FCSTD DOCUMENT  (FreeCAD 1.0R39109 (Git))
Label: seat_mover
License: All rights reserved
LicenseURL: https://en.wikipedia.org/wiki/All_rights_reserved
objects: App::Link×73, App::FeaturePython×3, Assembly::AssemblyLink×3, Assembly::JointGroup×1, Assembly::AssemblyObject×1
EXTERNAL_REF file=surge_platform.FCStd obj=Assembly
EXTERNAL_REF file=surge_platform.FCStd obj=linear_shaft_25x500
EXTERNAL_REF file=surge_platform.FCStd obj=linear_shaft_25x501
EXTERNAL_REF file=surge_platform.FCStd obj=SHF25
EXTERNAL_REF file=surge_platform.FCStd obj=SHF026
EXTERNAL_REF file=surge_platform.FCStd obj=SHF027
EXTERNAL_REF file=surge_platform.FCStd obj=SHF028
EXTERNAL_REF file=surge_platform.FCStd obj=_0ST_M02438
EXTERNAL_REF file=surge_platform.FCStd obj=SFU1605_ball_screw_250mm
EXTERNAL_REF file=surge_platform.FCStd obj=BK12
EXTERNAL_REF file=surge_platform.FCStd obj=coupler_10x19
EXTERNAL_REF file=surge_platform.FCStd obj=profile_40x40x500
EXTERNAL_REF file=surge_platform.FCStd obj=profile_40x40x501
EXTERNAL_REF file=surge_platform.FCStd obj=corner_bracket_40x40
EXTERNAL_REF file=surge_platform.FCStd obj=corner_bracket_40x041
EXTERNAL_REF file=surge_platform.FCStd obj=corner_bracket_40x042
EXTERNAL_REF file=surge_platform.FCStd obj=corner_bracket_40x043
EXTERNAL_REF file=sway_platform.FCStd obj=Assembly
EXTERNAL_REF file=sway_platform.FCStd obj=SC25UU_to_SH25
EXTERNAL_REF file=sway_platform.FCStd obj=SC25UU_to_SH026
EXTERNAL_REF file=sway_platform.FCStd obj=SC25UU
EXTERNAL_REF file=sway_platform.FCStd obj=SC25UU001
EXTERNAL_REF file=sway_platform.FCStd obj=SC25UU002
EXTERNAL_REF file=sway_platform.FCStd obj=SC25UU003
EXTERNAL_REF file=sway_platform.FCStd obj=SH25
EXTERNAL_REF file=sway_platform.FCStd obj=SH026
EXTERNAL_REF file=sway_platform.FCStd obj=SH027
EXTERNAL_REF file=sway_platform.FCStd obj=SH028
EXTERNAL_REF file=sway_platform.FCStd obj=linear_shaft_25x428
EXTERNAL_REF file=sway_platform.FCStd obj=linear_shaft_25x429
EXTERNAL_REF file=sway_platform.FCStd obj=SH029
EXTERNAL_REF file=sway_platform.FCStd obj=DSG16H_to_SH25
EXTERNAL_REF file=sway_platform.FCStd obj=DSG16H
EXTERNAL_REF file=sway_platform.FCStd obj=SFU1605_ball_screw_nut
EXTERNAL_REF file=sway_platform.FCStd obj=_0ST_M02438
EXTERNAL_REF file=sway_platform.FCStd obj=coupler_10x19
EXTERNAL_REF file=sway_platform.FCStd obj=SFU1605_ball_screw_250mm
EXTERNAL_REF file=sway_platform.FCStd obj=BK12
EXTERNAL_REF file=seat_platform.FCStd obj=Assembly
EXTERNAL_REF file=seat_platform.FCStd obj=SC25UU
EXTERNAL_REF file=seat_platform.FCStd obj=SC25UU001
EXTERNAL_REF file=seat_platform.FCStd obj=SC25UU002
EXTERNAL_REF file=seat_platform.FCStd obj=SC25UU003
EXTERNAL_REF file=seat_platform.FCStd obj=profile_40x40x310
EXTERNAL_REF file=seat_platform.FCStd obj=profile_40x40x311
EXTERNAL_REF file=seat_platform.FCStd obj=corner_bracket_40x40
EXTERNAL_REF file=seat_platform.FCStd obj=corner_bracket_40x041
EXTERNAL_REF file=seat_platform.FCStd obj=corner_bracket_40x042
EXTERNAL_REF file=seat_platform.FCStd obj=corner_bracket_40x043
EXTERNAL_REF file=seat_platform.FCStd obj=corner_bracket_40x044
EXTERNAL_REF file=seat_platform.FCStd obj=corner_bracket_40x045
EXTERNAL_REF file=seat_platform.FCStd obj=corner_bracket_40x046
EXTERNAL_REF file=seat_platform.FCStd obj=corner_bracket_40x047
EXTERNAL_REF file=seat_platform.FCStd obj=DSG16H_to_profile_40x40
EXTERNAL_REF file=seat_platform.FCStd obj=DSG16H
EXTERNAL_REF file=seat_platform.FCStd obj=SFU1605_ball_screw_nut
EXTERNAL_REF file=seat_platform.FCStd obj=profile_40x40x270
EXTERNAL_REF file=seat_platform.FCStd obj=profile_40x40x312
EXTERNAL_REF file=seat_platform.FCStd obj=corner_bracket_40x048
EXTERNAL_REF file=seat_platform.FCStd obj=corner_bracket_40x049
EXTERNAL_REF file=seat_platform.FCStd obj=corner_bracket_40x050
EXTERNAL_REF file=seat_platform.FCStd obj=corner_bracket_40x051
EXTERNAL_REF file=seat_platform.FCStd obj=seat
EXTERNAL_REF file=surge_platform.FCStd obj=surge_motor_mount_side
EXTERNAL_REF file=surge_platform.FCStd obj=surge_motor_mount_bottom
EXTERNAL_REF file=surge_platform.FCStd obj=surge_motor_mount_top
EXTERNAL_REF file=sway_platform.FCStd obj=sway_SC25UU_to_SH25_with_plate
EXTERNAL_REF file=sway_platform.FCStd obj=sway_motor_mount_rear_plate
EXTERNAL_REF file=sway_platform.FCStd obj=sway_SC25UU_to_SH25_with_plate001
EXTERNAL_REF file=sway_platform.FCStd obj=sway_motor_mount_front_plate
EXTERNAL_REF file=sway_platform.FCStd obj=sway_motor_mount_front_plate_shaft_support
EXTERNAL_REF file=sway_platform.FCStd obj=sway_motor_mount_side
EXTERNAL_REF file=sway_platform.FCStd obj=sway_motor_mount_top
EXTERNAL_REF file=sway_platform.FCStd obj=sway_motor_mount_bottom
EXTERNAL_REF file=surge_platform.FCStd obj=surge_BK12_mount_bottom
EXTERNAL_REF file=surge_platform.FCStd obj=surge_BK12_mount_top

FEATURE [App::Link] linear_shaft_25x500  label="linear_shaft_25x500_right"
  LinkPlacement = pos=(404,2.64e-14,1.8225e-12) rot=(0,0,1;0rad)
  LinkedObject = -> <external surge_platform.FCStd>#linear_shaft_25x500
  Placement = pos=(404,2.64e-14,1.8225e-12) rot=(0,0,1;0rad)
FEATURE [App::Link] linear_shaft_25x501  label="linear_shaft_25x50_left"
  LinkPlacement = pos=(0,0,1.819e-12) rot=(0,0,1;0rad)
  LinkedObject = -> <external surge_platform.FCStd>#linear_shaft_25x501
  Placement = pos=(0,0,1.819e-12) rot=(0,0,1;0rad)
FEATURE [App::Link] SHF25  label="SHF25_000"
  LinkPlacement = pos=(10,-527.778,-1.55556) rot=(0,0.707107,0.707107;3.14159rad)
  LinkedObject = -> <external surge_platform.FCStd>#SHF25
  Placement = pos=(10,-527.778,-1.55556) rot=(0,0.707107,0.707107;3.14159rad)
FEATURE [App::Link] SHF026  label="SHF25_001"
  LinkPlacement = pos=(-10,27.7778,-1.55556) rot=(1,0,0;1.5708rad)
  LinkedObject = -> <external surge_platform.FCStd>#SHF026
  Placement = pos=(-10,27.7778,-1.55556) rot=(1,0,0;1.5708rad)
FEATURE [App::Link] SHF027  label="SHF25_002"
  LinkPlacement = pos=(414,-527.778,-1.55556) rot=(0,0.707107,0.707107;3.14159rad)
  LinkedObject = -> <external surge_platform.FCStd>#SHF027
  Placement = pos=(414,-527.778,-1.55556) rot=(0,0.707107,0.707107;3.14159rad)
FEATURE [App::Link] SHF028  label="SHF25_003"
  LinkPlacement = pos=(394,27.7778,-1.55556) rot=(1,0,0;1.5708rad)
  LinkedObject = -> <external surge_platform.FCStd>#SHF028
  Placement = pos=(394,27.7778,-1.55556) rot=(1,0,0;1.5708rad)
FEATURE [App::Link] _0ST_M02438  label="80ST-M02438"
  LinkPlacement = pos=(202,-341.4,4.5) rot=(-1,0,0;1.5708rad)
  LinkedObject = -> <external surge_platform.FCStd>#_0ST_M02438
  Placement = pos=(202,-341.4,4.5) rot=(-1,0,0;1.5708rad)
FEATURE [App::Link] SFU1605_ball_screw_250mm
  LinkPlacement = pos=(202,-492.9,4.5) rot=(1,0,0;1.5708rad)
  LinkedObject = -> <external surge_platform.FCStd>#SFU1605_ball_screw_250mm
  Placement = pos=(202,-492.9,4.5) rot=(1,0,0;1.5708rad)
FEATURE [App::Link] BK12
  LinkPlacement = pos=(202,-235.65,-20.5) rot=(0,0,1;0rad)
  LinkedObject = -> <external surge_platform.FCStd>#BK12
  Placement = pos=(202,-235.65,-20.5) rot=(0,0,1;0rad)
FEATURE [App::Link] coupler_10x19
  LinkPlacement = pos=(202,-261.9,4.5) rot=(0,0,1;0rad)
  LinkedObject = -> <external surge_platform.FCStd>#coupler_10x19
  Placement = pos=(202,-261.9,4.5) rot=(0,0,1;0rad)
FEATURE [App::Link] profile_40x40x500  label="profile_40x40x500_right"
  LinkPlacement = pos=(262,-150,1.783e-12) rot=(0,0.707107,-0.707107;3.14159rad)
  LinkedObject = -> <external surge_platform.FCStd>#profile_40x40x500
  Placement = pos=(262,-150,1.783e-12) rot=(0,0.707107,-0.707107;3.14159rad)
FEATURE [App::Link] profile_40x40x501  label="profile_40x40x500_left"
  LinkPlacement = pos=(142,-150,1.783e-12) rot=(0,0.707107,-0.707107;3.14159rad)
  LinkedObject = -> <external surge_platform.FCStd>#profile_40x40x501
  Placement = pos=(142,-150,1.783e-12) rot=(0,0.707107,-0.707107;3.14159rad)
FEATURE [App::Link] corner_bracket_40x40  label="corner_bracket_40x40_000"
  LinkPlacement = pos=(142,-587.433,56) rot=(0,1,0;1.5708rad)
  LinkedObject = -> <external surge_platform.FCStd>#corner_bracket_40x40
  Placement = pos=(142,-587.433,56) rot=(0,1,0;1.5708rad)
FEATURE [App::Link] corner_bracket_40x041  label="corner_bracket_40x40_001"
  LinkPlacement = pos=(142,-36,-67.4326) rot=(0.57735,0.57735,0.57735;2.0944rad)
  LinkedObject = -> <external surge_platform.FCStd>#corner_bracket_40x041
  Placement = pos=(142,-36,-67.4326) rot=(0.57735,0.57735,0.57735;2.0944rad)
FEATURE [App::Link] corner_bracket_40x042  label="corner_bracket_40x40_002"
  LinkPlacement = pos=(262,-587.433,56) rot=(0,1,0;1.5708rad)
  LinkedObject = -> <external surge_platform.FCStd>#corner_bracket_40x042
  Placement = pos=(262,-587.433,56) rot=(0,1,0;1.5708rad)
FEATURE [App::Link] corner_bracket_40x043  label="corner_bracket_40x40_003"
  LinkPlacement = pos=(262,-36,67.4326) rot=(0.57735,0.57735,-0.57735;4.18879rad)
  LinkedObject = -> <external surge_platform.FCStd>#corner_bracket_40x043
  Placement = pos=(262,-36,67.4326) rot=(0.57735,0.57735,-0.57735;4.18879rad)
FEATURE [App::Link] SC25UU_to_SH25  label="SC25UU_to_SH25_000"
  LinkedObject = -> <external sway_platform.FCStd>#SC25UU_to_SH25
FEATURE [App::Link] SC25UU_to_SH026  label="SC25UU_to_SH25_001"
  LinkPlacement = pos=(1e-15,204,-1e-16) rot=(0,0,1;0rad)
  LinkedObject = -> <external sway_platform.FCStd>#SC25UU_to_SH026
  Placement = pos=(1e-15,204,-1e-16) rot=(0,0,1;0rad)
FEATURE [App::Link] SC25UU  label="SC25UU_000"
  LinkPlacement = pos=(38,67,-415.5) rot=(1,0,0;1.5708rad)
  LinkedObject = -> <external sway_platform.FCStd>#SC25UU
  Placement = pos=(38,67,-415.5) rot=(1,0,0;1.5708rad)
FEATURE [App::Link] SC25UU001  label="SC25UU_001"
  LinkPlacement = pos=(38,271,-415.5) rot=(1,0,0;1.5708rad)
  LinkedObject = -> <external sway_platform.FCStd>#SC25UU001
  Placement = pos=(38,271,-415.5) rot=(1,0,0;1.5708rad)
FEATURE [App::Link] SC25UU002  label="SC25UU_002"
  LinkPlacement = pos=(442,67,-415.5) rot=(1,0,0;1.5708rad)
  LinkedObject = -> <external sway_platform.FCStd>#SC25UU002
  Placement = pos=(442,67,-415.5) rot=(1,0,0;1.5708rad)
FEATURE [App::Link] SC25UU003  label="SC25UU_003"
  LinkPlacement = pos=(442,271,-415.5) rot=(1,0,0;1.5708rad)
  LinkedObject = -> <external sway_platform.FCStd>#SC25UU003
  Placement = pos=(442,271,-415.5) rot=(1,0,0;1.5708rad)
FEATURE [App::Link] SH25  label="SH25_000"
  LinkPlacement = pos=(-901.062,343.027,-226.938) rot=(0,0,1;0rad)
  LinkedObject = -> <external sway_platform.FCStd>#SH25
  Placement = pos=(-901.062,343.027,-226.938) rot=(0,0,1;0rad)
FEATURE [App::Link] SH026  label="SH25_001"
  LinkPlacement = pos=(977.062,-72.0272,-226.938) rot=(0,0,1;3.14159rad)
  LinkedObject = -> <external sway_platform.FCStd>#SH026
  Placement = pos=(977.062,-72.0272,-226.938) rot=(0,0,1;3.14159rad)
FEATURE [App::Link] SH027  label="SH25_002"
  LinkPlacement = pos=(-497.062,343.027,-226.938) rot=(0,0,1;0rad)
  LinkedObject = -> <external sway_platform.FCStd>#SH027
  Placement = pos=(-497.062,343.027,-226.938) rot=(0,0,1;0rad)
FEATURE [App::Link] SH028  label="SH25_003"
  LinkPlacement = pos=(1381.06,-72.0272,-226.938) rot=(0,0,1;3.14159rad)
  LinkedObject = -> <external sway_platform.FCStd>#SH028
  Placement = pos=(1381.06,-72.0272,-226.938) rot=(0,0,1;3.14159rad)
FEATURE [App::Link] linear_shaft_25x428  label="linear_shaft_25x428_front"
  LinkPlacement = pos=(454,33.5,45) rot=(0,0,-1;1.5708rad)
  LinkedObject = -> <external sway_platform.FCStd>#linear_shaft_25x428
  Placement = pos=(454,33.5,45) rot=(0,0,-1;1.5708rad)
FEATURE [App::Link] linear_shaft_25x429  label="linear_shaft_25x428_rear"
  LinkPlacement = pos=(454,237.5,45) rot=(0.707107,0.707107,0;3.14159rad)
  LinkedObject = -> <external sway_platform.FCStd>#linear_shaft_25x429
  Placement = pos=(454,237.5,45) rot=(0.707107,0.707107,0;3.14159rad)
FEATURE [App::Link] SH029  label="SH25_004"
  LinkPlacement = pos=(1179.06,-72.0272,-226.938) rot=(0,0,1;3.14159rad)
  LinkedObject = -> <external sway_platform.FCStd>#SH029
  Placement = pos=(1179.06,-72.0272,-226.938) rot=(0,0,1;3.14159rad)
FEATURE [App::Link] DSG16H_to_SH25
  LinkPlacement = pos=(215,218.5,-2) rot=(0,0,1;0rad)
  LinkedObject = -> <external sway_platform.FCStd>#DSG16H_to_SH25
  Placement = pos=(215,218.5,-2) rot=(0,0,1;0rad)
FEATURE [App::Link] DSG16H
  LinkPlacement = pos=(240,217.5,-22) rot=(0,0,1;0rad)
  LinkedObject = -> <external sway_platform.FCStd>#DSG16H
  Placement = pos=(240,217.5,-22) rot=(0,0,1;0rad)
FEATURE [App::Link] SFU1605_ball_screw_nut
  LinkPlacement = pos=(240,207.25,-22) rot=(0,-1,0;1.5708rad)
  LinkedObject = -> <external sway_platform.FCStd>#SFU1605_ball_screw_nut
  Placement = pos=(240,207.25,-22) rot=(0,-1,0;1.5708rad)
FEATURE [App::Link] _0ST_M02439  label="80ST-M02439"
  LinkPlacement = pos=(342.4,135.5,30) rot=(0.57735,-0.57735,-0.57735;2.0944rad)
  LinkedObject = -> <external sway_platform.FCStd>#_0ST_M02438
  Placement = pos=(342.4,135.5,30) rot=(0.57735,-0.57735,-0.57735;2.0944rad)
FEATURE [App::Link] coupler_10x020
  LinkPlacement = pos=(266.25,135.5,30) rot=(-0.57735,0.57735,0.57735;2.0944rad)
  LinkedObject = -> <external sway_platform.FCStd>#coupler_10x19
  Placement = pos=(266.25,135.5,30) rot=(-0.57735,0.57735,0.57735;2.0944rad)
FEATURE [App::Link] SFU1605_ball_screw_250mm001
  LinkPlacement = pos=(497.25,135.5,30) rot=(0.57735,0.57735,0.57735;2.0944rad)
  LinkedObject = -> <external sway_platform.FCStd>#SFU1605_ball_screw_250mm
  Placement = pos=(497.25,135.5,30) rot=(0.57735,0.57735,0.57735;2.0944rad)
FEATURE [App::Link] BK013
  LinkPlacement = pos=(240,135.5,55) rot=(0.707107,-0.707107,0;3.14159rad)
  LinkedObject = -> <external sway_platform.FCStd>#BK12
  Placement = pos=(240,135.5,55) rot=(0.707107,-0.707107,0;3.14159rad)
FEATURE [App::Link] SC25UU004  label="SC25UU_004"
  LinkPlacement = pos=(0,0,0) rot=(-0.57735,0.57735,0.57735;4.18879rad)
  LinkedObject = -> <external seat_platform.FCStd>#SC25UU
  Placement = pos=(0,0,0) rot=(-0.57735,0.57735,0.57735;4.18879rad)
FEATURE [App::Link] SC25UU005  label="SC25UU_005"
  LinkPlacement = pos=(-67,204,1.40432e-05) rot=(0.57735,0.57735,0.57735;2.0944rad)
  LinkedObject = -> <external seat_platform.FCStd>#SC25UU001
  Placement = pos=(-67,204,1.40432e-05) rot=(0.57735,0.57735,0.57735;2.0944rad)
FEATURE [App::Link] SC25UU006  label="SC25UU_006"
  LinkPlacement = pos=(136,-2.07725e-07,-2.78731e-05) rot=(0.57735,0.57735,0.57735;2.0944rad)
  LinkedObject = -> <external seat_platform.FCStd>#SC25UU002
  Placement = pos=(136,-2.07725e-07,-2.78731e-05) rot=(0.57735,0.57735,0.57735;2.0944rad)
FEATURE [App::Link] SC25UU007  label="SC25UU_007"
  LinkPlacement = pos=(203,204,-4.12931e-05) rot=(-0.57735,0.57735,0.57735;4.18879rad)
  LinkedObject = -> <external seat_platform.FCStd>#SC25UU003
  Placement = pos=(203,204,-4.12931e-05) rot=(-0.57735,0.57735,0.57735;4.18879rad)
FEATURE [App::Link] profile_40x40x310  label="profile_40x40x310_right"
  LinkPlacement = pos=(183,107,435.5) rot=(1,0,0;1.5708rad)
  LinkedObject = -> <external seat_platform.FCStd>#profile_40x40x310
  Placement = pos=(183,107,435.5) rot=(1,0,0;1.5708rad)
FEATURE [App::Link] profile_40x40x311  label="profile_40x40x310_left"
  LinkPlacement = pos=(-46.9999,107,435.5) rot=(1,0,0;1.5708rad)
  LinkedObject = -> <external seat_platform.FCStd>#profile_40x40x311
  Placement = pos=(-46.9999,107,435.5) rot=(1,0,0;1.5708rad)
FEATURE [App::Link] corner_bracket_40x044  label="corner_bracket_40x40_004"
  LinkPlacement = pos=(9.00006,-27,328.067) rot=(0,0.707107,0.707107;3.14159rad)
  LinkedObject = -> <external seat_platform.FCStd>#corner_bracket_40x40
  Placement = pos=(9.00006,-27,328.067) rot=(0,0.707107,0.707107;3.14159rad)
FEATURE [App::Link] corner_bracket_40x045  label="corner_bracket_40x40_005"
  LinkPlacement = pos=(9.00006,27,328.067) rot=(0,0.707107,0.707107;3.14159rad)
  LinkedObject = -> <external seat_platform.FCStd>#corner_bracket_40x041
  Placement = pos=(9.00006,27,328.067) rot=(0,0.707107,0.707107;3.14159rad)
FEATURE [App::Link] corner_bracket_40x046  label="corner_bracket_40x40_006"
  LinkPlacement = pos=(9.00006,177,328.067) rot=(0,0.707107,0.707107;3.14159rad)
  LinkedObject = -> <external seat_platform.FCStd>#corner_bracket_40x042
  Placement = pos=(9.00006,177,328.067) rot=(0,0.707107,0.707107;3.14159rad)
FEATURE [App::Link] corner_bracket_40x047  label="corner_bracket_40x40_007"
  LinkPlacement = pos=(9.00006,231,328.067) rot=(0,0.707107,0.707107;3.14159rad)
  LinkedObject = -> <external seat_platform.FCStd>#corner_bracket_40x043
  Placement = pos=(9.00006,231,328.067) rot=(0,0.707107,0.707107;3.14159rad)
FEATURE [App::Link] corner_bracket_40x048  label="corner_bracket_40x40_008"
  LinkPlacement = pos=(127,-27,328.067) rot=(1,0,0;1.5708rad)
  LinkedObject = -> <external seat_platform.FCStd>#corner_bracket_40x044
  Placement = pos=(127,-27,328.067) rot=(1,0,0;1.5708rad)
FEATURE [App::Link] corner_bracket_40x049  label="corner_bracket_40x40_009"
  LinkPlacement = pos=(127,27,328.067) rot=(1,0,0;1.5708rad)
  LinkedObject = -> <external seat_platform.FCStd>#corner_bracket_40x045
  Placement = pos=(127,27,328.067) rot=(1,0,0;1.5708rad)
FEATURE [App::Link] corner_bracket_40x050  label="corner_bracket_40x40_010"
  LinkPlacement = pos=(250.433,177,451.5) rot=(-0.57735,0.57735,0.57735;2.0944rad)
  LinkedObject = -> <external seat_platform.FCStd>#corner_bracket_40x046
  Placement = pos=(250.433,177,451.5) rot=(-0.57735,0.57735,0.57735;2.0944rad)
FEATURE [App::Link] corner_bracket_40x051  label="corner_bracket_40x40_011"
  LinkPlacement = pos=(250.433,231,451.5) rot=(-0.57735,0.57735,0.57735;2.0944rad)
  LinkedObject = -> <external seat_platform.FCStd>#corner_bracket_40x047
  Placement = pos=(250.433,231,451.5) rot=(-0.57735,0.57735,0.57735;2.0944rad)
FEATURE [App::Link] DSG16H_to_profile_40x40
  LinkPlacement = pos=(-27.9999,77,394) rot=(0,0,1;1.5708rad)
  LinkedObject = -> <external seat_platform.FCStd>#DSG16H_to_profile_40x40
  Placement = pos=(-27.9999,77,394) rot=(0,0,1;1.5708rad)
FEATURE [App::Link] DSG16H001
  LinkPlacement = pos=(-26.9999,102,374) rot=(0,0,1;1.5708rad)
  LinkedObject = -> <external seat_platform.FCStd>#DSG16H
  Placement = pos=(-26.9999,102,374) rot=(0,0,1;1.5708rad)
FEATURE [App::Link] SFU1605_ball_screw_nut001
  LinkPlacement = pos=(-16.7499,102,374) rot=(0.57735,-0.57735,0.57735;2.0944rad)
  LinkedObject = -> <external seat_platform.FCStd>#SFU1605_ball_screw_nut
  Placement = pos=(-16.7499,102,374) rot=(0.57735,-0.57735,0.57735;2.0944rad)
FEATURE [App::FeaturePython] Joint  label="Slider_sway_platform"  # Assembly joint (typed FeaturePython)
  Activated = true
  AngleMax = 0
  AngleMin = 0
  Detach1 = false
  Detach2 = false
  Distance = 0
  Distance2 = 0
  EnableAngleMax = false
  EnableAngleMin = false
  EnableLengthMax = true
  EnableLengthMin = true
  JointType = 3 (Slider)
  LengthMax = -14.5
  LengthMin = -141
  Placement1 = pos=(-1.42e-14,389,33.5) rot=(0,0,1;0rad)
  Placement2 = pos=(0,-250,5.5e-14) rot=(1,0,0;1.5708rad)
  Reference1 = -> Assembly [sway_platform.SC25UU.Face24,sway_platform.SC25UU.Face24]
  Reference2 = -> Assembly [surge_platform.linear_shaft_25x501.Face1,surge_platform.linear_shaft_25x501.Face1]
FEATURE [App::FeaturePython] Joint001  label="Slider_seat_platform"  # Assembly joint (typed FeaturePython)
  Activated = true
  AngleMax = 0
  AngleMin = 0
  Detach1 = false
  Detach2 = false
  Distance = 0
  Distance2 = 0
  EnableAngleMax = false
  EnableAngleMin = false
  EnableLengthMax = true
  EnableLengthMin = true
  JointType = 3 (Slider)
  LengthMax = -47.5
  LengthMin = -155.5
  Placement1 = pos=(-8.5e-15,389,33.5) rot=(0,0,1;0rad)
  Placement2 = pos=(0,-214,4.26e-14) rot=(1,0,0;1.5708rad)
  Reference1 = -> Assembly [seat_platform.SC25UU004.Face24,seat_platform.SC25UU004.Face24]
  Reference2 = -> Assembly [sway_platform.linear_shaft_25x428.Face1,sway_platform.linear_shaft_25x428.Face1]
FEATURE [App::Link] profile_40x40x270  label="profile_40x40x270_front"
  LinkPlacement = pos=(53.0001,-33,475.5) rot=(-0.57735,0.57735,0.57735;4.18879rad)
  LinkedObject = -> <external seat_platform.FCStd>#profile_40x40x270
  Placement = pos=(53.0001,-33,475.5) rot=(-0.57735,0.57735,0.57735;4.18879rad)
FEATURE [App::Link] profile_40x40x312  label="profile_40x40x270_back"
  LinkPlacement = pos=(53.0001,237,475.5) rot=(-0.57735,0.57735,0.57735;4.18879rad)
  LinkedObject = -> <external seat_platform.FCStd>#profile_40x40x312
  Placement = pos=(53.0001,237,475.5) rot=(-0.57735,0.57735,0.57735;4.18879rad)
FEATURE [App::Link] corner_bracket_40x052  label="corner_bracket_40x40_012"
  LinkPlacement = pos=(-46.9999,23,368.067) rot=(-0.57735,0.57735,0.57735;4.18879rad)
  LinkedObject = -> <external seat_platform.FCStd>#corner_bracket_40x048
  Placement = pos=(-46.9999,23,368.067) rot=(-0.57735,0.57735,0.57735;4.18879rad)
FEATURE [App::Link] corner_bracket_40x053  label="corner_bracket_40x40_013"
  LinkPlacement = pos=(-46.9999,304.433,491.5) rot=(-0.707107,0,0.707107;3.14159rad)
  LinkedObject = -> <external seat_platform.FCStd>#corner_bracket_40x049
  Placement = pos=(-46.9999,304.433,491.5) rot=(-0.707107,0,0.707107;3.14159rad)
FEATURE [App::Link] corner_bracket_40x054  label="corner_bracket_40x40_014"
  LinkPlacement = pos=(183,-100.433,491.5) rot=(0,1,0;1.5708rad)
  LinkedObject = -> <external seat_platform.FCStd>#corner_bracket_40x050
  Placement = pos=(183,-100.433,491.5) rot=(0,1,0;1.5708rad)
FEATURE [App::Link] corner_bracket_40x055  label="corner_bracket_40x40_015"
  LinkPlacement = pos=(183,181,368.067) rot=(0.57735,0.57735,0.57735;2.0944rad)
  LinkedObject = -> <external seat_platform.FCStd>#corner_bracket_40x051
  Placement = pos=(183,181,368.067) rot=(0.57735,0.57735,0.57735;2.0944rad)
FEATURE [App::Link] seat
  LinkPlacement = pos=(68.0001,-137,495.5) rot=(1,0,0;1.5708rad)
  LinkedObject = -> <external seat_platform.FCStd>#seat
  Placement = pos=(68.0001,-137,495.5) rot=(1,0,0;1.5708rad)
FEATURE [Assembly::AssemblyLink] seat_platform
  Group = -> [SC25UU004,SC25UU005,SC25UU006,SC25UU007,profile_40x40x310,profile_40x40x311,corner_bracket_40x044,corner_bracket_40x045,corner_bracket_40x046,corner_bracket_40x047,corner_bracket_40x048,corner_bracket_40x049,corner_bracket_40x050,corner_bracket_40x051,DSG16H_to_profile_40x40,DSG16H001,SFU1605_ball_screw_nut001,profile_40x40x270,profile_40x40x312,corner_bracket_40x052,corner_bracket_40x053,+3 more]
  LinkedObject = -> <external seat_platform.FCStd>#Assembly
  Origin = -> Origin003
  Placement = pos=(112.107,-391,-317.5) rot=(-0.007475,-1.00311,0.007476;0rad)
  Rigid = true
FEATURE [App::Link] surge_motor_mount_side
  LinkPlacement = pos=(202.065,-333.4,-0.05) rot=(0,0,1;3.14159rad)
  LinkedObject = -> <external surge_platform.FCStd>#surge_motor_mount_side
  Placement = pos=(202.065,-333.4,-0.05) rot=(0,0,1;3.14159rad)
FEATURE [App::Link] surge_motor_mount_bottom
  LinkPlacement = pos=(202,-410,1.7302e-12) rot=(0,0,1;0rad)
  LinkedObject = -> <external surge_platform.FCStd>#surge_motor_mount_bottom
  Placement = pos=(202,-410,1.7302e-12) rot=(0,0,1;0rad)
FEATURE [App::Link] surge_motor_mount_top
  LinkPlacement = pos=(202,-410,1.7124e-12) rot=(0,0,1;0rad)
  LinkedObject = -> <external surge_platform.FCStd>#surge_motor_mount_top
  Placement = pos=(202,-410,1.7124e-12) rot=(0,0,1;0rad)
FEATURE [App::Link] sway_SC25UU_to_SH25_with_plate  label="sway_SC25UU_to_SH25_with_plate_001"
  LinkPlacement = pos=(404,204,3e-16) rot=(0,0,1;0rad)
  LinkedObject = -> <external sway_platform.FCStd>#sway_SC25UU_to_SH25_with_plate
  Placement = pos=(404,204,3e-16) rot=(0,0,1;0rad)
FEATURE [App::Link] sway_motor_mount_rear_plate
  LinkPlacement = pos=(430,272.5,5) rot=(0,0,1;3.14159rad)
  LinkedObject = -> <external sway_platform.FCStd>#sway_motor_mount_rear_plate
  Placement = pos=(430,272.5,5) rot=(0,0,1;3.14159rad)
FEATURE [App::Link] sway_SC25UU_to_SH25_with_plate001  label="sway_SC25UU_to_SH25_with_plate_000"
  LinkPlacement = pos=(404,-1e-16,3e-16) rot=(0,0,1;0rad)
  LinkedObject = -> <external sway_platform.FCStd>#sway_SC25UU_to_SH25_with_plate001
  Placement = pos=(404,-1e-16,3e-16) rot=(0,0,1;0rad)
FEATURE [App::Link] sway_motor_mount_front_plate
  LinkPlacement = pos=(430,68.5,5) rot=(0,0,1;3.14159rad)
  LinkedObject = -> <external sway_platform.FCStd>#sway_motor_mount_front_plate
  Placement = pos=(430,68.5,5) rot=(0,0,1;3.14159rad)
FEATURE [App::Link] sway_motor_mount_front_plate_shaft_support
  LinkPlacement = pos=(252,33.5,45) rot=(0,0,1;3.14159rad)
  LinkedObject = -> <external sway_platform.FCStd>#sway_motor_mount_front_plate_shaft_support
  Placement = pos=(252,33.5,45) rot=(0,0,1;3.14159rad)
FEATURE [App::Link] sway_motor_mount_side
  LinkPlacement = pos=(334.4,135.565,9.95) rot=(0,0,-1;1.5708rad)
  LinkedObject = -> <external sway_platform.FCStd>#sway_motor_mount_side
  Placement = pos=(334.4,135.565,9.95) rot=(0,0,-1;1.5708rad)
FEATURE [App::Link] sway_motor_mount_top
  LinkPlacement = pos=(434,135.5,10) rot=(0,0,1;1.5708rad)
  LinkedObject = -> <external sway_platform.FCStd>#sway_motor_mount_top
  Placement = pos=(434,135.5,10) rot=(0,0,1;1.5708rad)
FEATURE [App::Link] sway_motor_mount_bottom
  LinkPlacement = pos=(419,135.5,10) rot=(0,0,-1;1.5708rad)
  LinkedObject = -> <external sway_platform.FCStd>#sway_motor_mount_bottom
  Placement = pos=(419,135.5,10) rot=(0,0,-1;1.5708rad)
FEATURE [Assembly::AssemblyLink] sway_platform
  Group = -> [SC25UU_to_SH25,SC25UU_to_SH026,SC25UU,SC25UU001,SC25UU002,SC25UU003,SH25,SH026,SH027,SH028,linear_shaft_25x428,linear_shaft_25x429,SH029,DSG16H_to_SH25,DSG16H,SFU1605_ball_screw_nut,_0ST_M02439,coupler_10x020,SFU1605_ball_screw_250mm001,BK013,sway_SC25UU_to_SH25_with_plate,sway_motor_mount_rear_plate,sway_SC25UU_to_SH25_with_plate001,sway_motor_mount_front_plate,+4 more]
  LinkedObject = -> <external sway_platform.FCStd>#Assembly
  Origin = -> Origin002
  Placement = pos=(-38,-424.5,26.5) rot=(0,0,1;0rad)
  Rigid = true
FEATURE [App::Link] surge_BK12_mount_bottom
  LinkPlacement = pos=(202,-223.15,4.92877e-10) rot=(0,0,1;0rad)
  LinkedObject = -> <external surge_platform.FCStd>#surge_BK12_mount_bottom
  Placement = pos=(202,-223.15,4.92877e-10) rot=(0,0,1;0rad)
FEATURE [App::Link] surge_BK12_mount_top
  LinkPlacement = pos=(202,-223.15,4.92873e-10) rot=(0,0,1;0rad)
  LinkedObject = -> <external surge_platform.FCStd>#surge_BK12_mount_top
  Placement = pos=(202,-223.15,4.92873e-10) rot=(0,0,1;0rad)
FEATURE [Assembly::AssemblyLink] surge_platform
  Group = -> [linear_shaft_25x500,linear_shaft_25x501,SHF25,SHF026,SHF027,SHF028,_0ST_M02438,SFU1605_ball_screw_250mm,BK12,coupler_10x19,profile_40x40x500,profile_40x40x501,corner_bracket_40x40,corner_bracket_40x041,corner_bracket_40x042,corner_bracket_40x043,surge_motor_mount_side,surge_motor_mount_bottom,surge_motor_mount_top,surge_BK12_mount_bottom,surge_BK12_mount_top]
  LinkedObject = -> <external surge_platform.FCStd>#Assembly
  Origin = -> Origin001
  Rigid = true
FEATURE [App::FeaturePython] GroundedJoint  label="GroundedJoint_surge_platform"  # Assembly grounded joint (typed FeaturePython)
  ObjectToGround = -> surge_platform
FEATURE [Assembly::JointGroup] Joints
  Group = -> [GroundedJoint,Joint,Joint001]
FEATURE [Assembly::AssemblyObject] Assembly  label="seat_mover"
  Group = -> [Joints,surge_platform,sway_platform,seat_platform,GroundedJoint,Joint,Joint001]
  Origin = -> Origin
  Type = Assembly

RESOLVED EXTERNAL PARTS (link-assembly join: the EXTERNAL_REF files above that resolve inside this repo's crawl, each included once):
---- part surge_platform.FCStd = doc fcstd_e89454650b1e ----
FCSTD DOCUMENT  (FreeCAD 1.0R39109 (Git))
Label: surge_platform
License: All rights reserved
LicenseURL: https://en.wikipedia.org/wiki/All_rights_reserved
objects: App::Link×21, App::FeaturePython×21, Assembly::JointGroup×1, Assembly::AssemblyObject×1
EXTERNAL_REF file=../parts_library/linear_shaft.FCStd obj=Body
EXTERNAL_REF file=../parts_library/SHF25.FCStd obj=Part__Feature
EXTERNAL_REF file=../parts_library/motor.FCStd obj=SERVOMOTOR_80ST_M02430
EXTERNAL_REF file=../parts_library/SFU1605.FCStd obj=SFU1605_250_v6
EXTERNAL_REF file=../parts_library/SFU1605.FCStd obj=BK12_v3
EXTERNAL_REF file=../parts_library/coupler.FCStd obj=Body
EXTERNAL_REF file=../parts_library/profile_40_serie.FCStd obj=Body003
EXTERNAL_REF file=../parts_library/corner_bracket_40x40.FCStd obj=Part__Feature
EXTERNAL_REF file=surge_motor_mount_side.FCStd obj=Body
EXTERNAL_REF file=surge_motor_mount_bottom.FCStd obj=Body
EXTERNAL_REF file=surge_motor_mount_top.FCStd obj=Body
EXTERNAL_REF file=surge_BK12_mount_bottom.FCStd obj=Body
EXTERNAL_REF file=surge_BK12_mount_top.FCStd obj=Body

FEATURE [App::Link] linear_shaft_25x500  label="linear_shaft_25x500_right"
  LinkPlacement = pos=(404,2.64e-14,1.8225e-12) rot=(0,0,1;0rad)
  LinkedObject = -> <external ../parts_library/linear_shaft.FCStd>#Body
  Placement = pos=(404,2.64e-14,1.8225e-12) rot=(0,0,1;0rad)
FEATURE [App::Link] linear_shaft_25x501  label="linear_shaft_25x500_left"
  LinkPlacement = pos=(0,0,1.819e-12) rot=(0,0,1;0rad)
  LinkedObject = -> <external ../parts_library/linear_shaft.FCStd>#Body
  Placement = pos=(0,0,1.819e-12) rot=(0,0,1;0rad)
FEATURE [App::FeaturePython] GroundedJoint  label="GroundedJoint_linear_shaft_25x500_left"  # Assembly grounded joint (typed FeaturePython)
  ObjectToGround = -> linear_shaft_25x501
  Placement = pos=(0,0,1.819e-12) rot=(0,0,1;0rad)
FEATURE [App::FeaturePython] Joint  label="Fixed_linear_shaft_25x500_right"  # Assembly joint (typed FeaturePython)
  Activated = true
  AngleMax = 0
  AngleMin = 0
  Detach1 = false
  Detach2 = false
  Distance = 0
  Distance2 = 0
  EnableAngleMax = false
  EnableAngleMin = false
  EnableLengthMax = false
  EnableLengthMin = false
  JointType = 0 (Fixed)
  LengthMax = 0
  LengthMin = 0
  Offset1 = pos=(404,0,0) rot=(0,0,1;0rad)
  Placement1 = pos=(404,-500,-1.137e-13) rot=(1,0,0;1.5708rad)
  Placement2 = pos=(0,-500,-1.172e-13) rot=(1,0,0;1.5708rad)
  Reference1 = -> Assembly [linear_shaft_25x501.Edge3,linear_shaft_25x501.Edge3]
  Reference2 = -> Assembly [linear_shaft_25x500.Edge3,linear_shaft_25x500.Edge3]
FEATURE [App::Link] SHF25  label="SHF25_000"
  LinkPlacement = pos=(10,-527.778,-1.55556) rot=(0,0.707107,0.707107;3.14159rad)
  LinkedObject = -> <external ../parts_library/SHF25.FCStd>#Part__Feature
  Placement = pos=(10,-527.778,-1.55556) rot=(0,0.707107,0.707107;3.14159rad)
FEATURE [App::Link] SHF026  label="SHF25_001"
  LinkPlacement = pos=(-10,27.7778,-1.55556) rot=(1,0,0;1.5708rad)
  LinkedObject = -> <external ../parts_library/SHF25.FCStd>#Part__Feature
  Placement = pos=(-10,27.7778,-1.55556) rot=(1,0,0;1.5708rad)
FEATURE [App::Link] SHF027  label="SHF25_002"
  LinkPlacement = pos=(414,-527.778,-1.55556) rot=(0,0.707107,0.707107;3.14159rad)
  LinkedObject = -> <external ../parts_library/SHF25.FCStd>#Part__Feature
  Placement = pos=(414,-527.778,-1.55556) rot=(0,0.707107,0.707107;3.14159rad)
FEATURE [App::Link] SHF028  label="SHF25_003"
  LinkPlacement = pos=(394,27.7778,-1.55556) rot=(1,0,0;1.5708rad)
  LinkedObject = -> <external ../parts_library/SHF25.FCStd>#Part__Feature
  Placement = pos=(394,27.7778,-1.55556) rot=(1,0,0;1.5708rad)
FEATURE [App::FeaturePython] Joint001  label="Fixed_SHF25_000"  # Assembly joint (typed FeaturePython)
  Activated = true
  AngleMax = 0
  AngleMin = 0
  Detach1 = false
  Detach2 = false
  Distance = 0
  Distance2 = 0
  EnableAngleMax = false
  EnableAngleMin = false
  EnableLengthMax = false
  EnableLengthMin = false
  JointType = 0 (Fixed)
  LengthMax = 0
  LengthMin = 0
  Offset2 = pos=(0,0,0) rot=(0,0,1;3.14159rad)
  Placement1 = pos=(0,-500,-1.137e-13) rot=(1,0,0;1.5708rad)
  Placement2 = pos=(10,1.55556,27.7778) rot=(0,0,1;3.14159rad)
  Reference1 = -> Assembly [linear_shaft_25x501.Edge3,linear_shaft_25x501.Edge3]
  Reference2 = -> Assembly [SHF25.Edge35,SHF25.Edge35]
FEATURE [App::FeaturePython] Joint002  label="Fixed_SHF25_001"  # Assembly joint (typed FeaturePython)
  Activated = true
  AngleMax = 0
  AngleMin = 0
  Detach1 = false
  Detach2 = false
  Distance = 0
  Distance2 = 0
  EnableAngleMax = false
  EnableAngleMin = false
  EnableLengthMax = false
  EnableLengthMin = false
  JointType = 0 (Fixed)
  LengthMax = 0
  LengthMin = 0
  Placement1 = pos=(0,0,0) rot=(1,0,0;1.5708rad)
  Placement2 = pos=(10,1.55556,27.7778) rot=(0,0,1;0rad)
  Reference1 = -> Assembly [linear_shaft_25x501.Edge2,linear_shaft_25x501.Edge2]
  Reference2 = -> Assembly [SHF026.Edge35,SHF026.Edge35]
FEATURE [App::FeaturePython] Joint003  label="Fixed_SHF25_002"  # Assembly joint (typed FeaturePython)
  Activated = true
  AngleMax = 0
  AngleMin = 0
  Detach1 = false
  Detach2 = false
  Distance = 0
  Distance2 = 0
  EnableAngleMax = false
  EnableAngleMin = false
  EnableLengthMax = false
  EnableLengthMin = false
  JointType = 0 (Fixed)
  LengthMax = 0
  LengthMin = 0
  Offset2 = pos=(0,0,0) rot=(0,0,1;3.14159rad)
  Placement1 = pos=(0,-500,-1.172e-13) rot=(1,0,0;1.5708rad)
  Placement2 = pos=(10,1.55556,27.7778) rot=(0,0,1;3.14159rad)
  Reference1 = -> Assembly [linear_shaft_25x500.Edge3,linear_shaft_25x500.Edge3]
  Reference2 = -> Assembly [SHF027.Edge35,SHF027.Edge35]
FEATURE [App::FeaturePython] Joint004  label="Fixed_SHF25_003"  # Assembly joint (typed FeaturePython)
  Activated = true
  AngleMax = 0
  AngleMin = 0
  Detach1 = false
  Detach2 = false
  Distance = 0
  Distance2 = 0
  EnableAngleMax = false
  EnableAngleMin = false
  EnableLengthMax = false
  EnableLengthMin = false
  JointType = 0 (Fixed)
  LengthMax = 0
  LengthMin = 0
  Placement1 = pos=(0,0,0) rot=(1,0,0;1.5708rad)
  Placement2 = pos=(10,1.55556,27.7778) rot=(0,0,1;0rad)
  Reference1 = -> Assembly [linear_shaft_25x500.Edge2,linear_shaft_25x500.Edge2]
  Reference2 = -> Assembly [SHF028.Edge35,SHF028.Edge35]
FEATURE [App::Link] _0ST_M02438  label="80ST-M02438"
  LinkPlacement = pos=(202,-341.4,4.5) rot=(-1,0,0;1.5708rad)
  LinkedObject = -> <external ../parts_library/motor.FCStd>#SERVOMOTOR_80ST_M02430
  Placement = pos=(202,-341.4,4.5) rot=(-1,0,0;1.5708rad)
FEATURE [App::FeaturePython] Joint005  label="Fixed_80ST-M02438"  # Assembly joint (typed FeaturePython)
  Activated = true
  AngleMax = 0
  AngleMin = 0
  Detach1 = false
  Detach2 = false
  Distance = 0
  Distance2 = 0
  EnableAngleMax = false
  EnableAngleMin = false
  EnableLengthMax = false
  EnableLengthMin = false
  JointType = 0 (Fixed)
  LengthMax = 0
  LengthMin = 0
  Offset1 = pos=(202,4.5,0) rot=(0,0,1;0rad)
  Offset2 = pos=(0,0,16) rot=(0,0,1;3.14159rad)
  Placement1 = pos=(202,-500,4.5) rot=(1,0,0;1.5708rad)
  Placement2 = pos=(0,0,-158.6) rot=(1,0,0;3.14159rad)
  Reference1 = -> Assembly [linear_shaft_25x501.Edge3,linear_shaft_25x501.Edge3]
  Reference2 = -> Assembly [_0ST_M02438.Part__Feature004.Edge14,_0ST_M02438.Part__Feature004.Edge14]
FEATURE [App::Link] SFU1605_ball_screw_250mm
  LinkPlacement = pos=(202,-492.9,4.5) rot=(1,0,0;1.5708rad)
  LinkedObject = -> <external ../parts_library/SFU1605.FCStd>#SFU1605_250_v6
  Placement = pos=(202,-492.9,4.5) rot=(1,0,0;1.5708rad)
FEATURE [App::Link] BK12
  LinkPlacement = pos=(202,-235.65,-20.5) rot=(0,0,1;0rad)
  LinkedObject = -> <external ../parts_library/SFU1605.FCStd>#BK12_v3
  Placement = pos=(202,-235.65,-20.5) rot=(0,0,1;0rad)
FEATURE [App::Link] coupler_10x19
  LinkPlacement = pos=(202,-261.9,4.5) rot=(0,0,1;0rad)
  LinkedObject = -> <external ../parts_library/coupler.FCStd>#Body
  Placement = pos=(202,-261.9,4.5) rot=(0,0,1;0rad)
FEATURE [App::FeaturePython] Joint006  label="Fixed_coupler_10x19"  # Assembly joint (typed FeaturePython)
  Activated = true
  AngleMax = 0
  AngleMin = 0
  Detach1 = false
  Detach2 = false
  Distance = 0
  Distance2 = 0
  EnableAngleMax = false
  EnableAngleMin = false
  EnableLengthMax = false
  EnableLengthMin = false
  JointType = 0 (Fixed)
  LengthMax = 0
  LengthMin = 0
  Offset2 = pos=(0,0,5) rot=(0,0,1;0rad)
  Placement1 = pos=(0,-31.5,-1.42e-14) rot=(1,0,0;1.5708rad)
  Placement2 = pos=(0,0,48) rot=(0,0,1;0rad)
  Reference1 = -> Assembly [coupler_10x19.Edge9,coupler_10x19.Edge9]
  Reference2 = -> Assembly [_0ST_M02438.Part__Feature002.Edge9,_0ST_M02438.Part__Feature002.Edge9]
FEATURE [App::FeaturePython] Joint008  label="Fixed_SFU1605_ball_screw_250mm"  # Assembly joint (typed FeaturePython)
  Activated = true
  AngleMax = 0
  AngleMin = 0
  Detach1 = false
  Detach2 = false
  Distance = 0
  Distance2 = 0
  EnableAngleMax = false
  EnableAngleMin = false
  EnableLengthMax = false
  EnableLengthMin = false
  JointType = 0 (Fixed)
  LengthMax = 0
  LengthMin = 0
  Offset2 = pos=(0,0,4) rot=(0,0,1;0rad)
  Placement1 = pos=(0,-18.5,-3.6e-15) rot=(-1,0,0;1.5708rad)
  Placement2 = pos=(2e-16,3e-16,4) rot=(0,0,1;0rad)
  Reference1 = -> Assembly [coupler_10x19.Edge7,coupler_10x19.Edge7]
  Reference2 = -> Assembly [SFU1605_ball_screw_250mm.Part__Feature110.Edge105,SFU1605_ball_screw_250mm.Part__Feature110.Edge105]
FEATURE [App::FeaturePython] Joint009  label="Fixed_BK12"  # Assembly joint (typed FeaturePython)
  Activated = true
  AngleMax = 0
  AngleMin = 0
  Detach1 = false
  Detach2 = false
  Distance = 0
  Distance2 = 0
  EnableAngleMax = false
  EnableAngleMin = false
  EnableLengthMax = false
  EnableLengthMin = false
  JointType = 0 (Fixed)
  LengthMax = 0
  LengthMin = 0
  Offset2 = pos=(0,0,0) rot=(0,0,1;3.14159rad)
  Placement1 = pos=(2e-16,3e-16,-53.75) rot=(0,0,1;0rad)
  Placement2 = pos=(1.1e-15,13,25) rot=(1,0,0;4.71239rad)
  Reference1 = -> Assembly [SFU1605_ball_screw_250mm.Part__Feature110.Edge52,SFU1605_ball_screw_250mm.Part__Feature110.Edge52]
  Reference2 = -> Assembly [BK12.Part__Feature030.Edge19,BK12.Part__Feature030.Edge19]
FEATURE [App::FeaturePython] Joint010  label="Fixed_profile_40x40x500_left"  # Assembly joint (typed FeaturePython)
  Activated = true
  AngleMax = 0
  AngleMin = 0
  Detach1 = false
  Detach2 = false
  Distance = 0
  Distance2 = 0
  EnableAngleMax = false
  EnableAngleMin = false
  EnableLengthMax = false
  EnableLengthMin = false
  JointType = 0 (Fixed)
  LengthMax = 0
  LengthMin = 0
  Offset1 = pos=(142,0,0) rot=(0,0,1;0rad)
  Placement1 = pos=(142,-500,-1.137e-13) rot=(1,0,0;1.5708rad)
  Placement2 = pos=(0,0,350) rot=(0,-1,0;3.14159rad)
  Reference1 = -> Assembly [linear_shaft_25x501.Edge3,linear_shaft_25x501.Edge3]
  Reference2 = -> Assembly [profile_40x40x501.Edge292,profile_40x40x501.Edge292]
FEATURE [App::Link] profile_40x40x500  label="profile_40x40x500_right"
  LinkPlacement = pos=(262,-150,1.783e-12) rot=(0,0.707107,-0.707107;3.14159rad)
  LinkedObject = -> <external ../parts_library/profile_40_serie.FCStd>#Body003
  Placement = pos=(262,-150,1.783e-12) rot=(0,0.707107,-0.707107;3.14159rad)
FEATURE [App::Link] profile_40x40x501  label="profile_40x40x500_left"
  LinkPlacement = pos=(142,-150,1.783e-12) rot=(0,0.707107,-0.707107;3.14159rad)
  LinkedObject = -> <external ../parts_library/profile_40_serie.FCStd>#Body003
  Placement = pos=(142,-150,1.783e-12) rot=(0,0.707107,-0.707107;3.14159rad)
FEATURE [App::Link] corner_bracket_40x40  label="corner_bracket_40x40_000"
  LinkPlacement = pos=(142,-587.433,56) rot=(0,1,0;1.5708rad)
  LinkedObject = -> <external ../parts_library/corner_bracket_40x40.FCStd>#Part__Feature
  Placement = pos=(142,-587.433,56) rot=(0,1,0;1.5708rad)
FEATURE [App::Link] corner_bracket_40x041  label="corner_bracket_40x40_001"
  LinkPlacement = pos=(142,-36,-67.4326) rot=(0.57735,0.57735,0.57735;2.0944rad)
  LinkedObject = -> <external ../parts_library/corner_bracket_40x40.FCStd>#Part__Feature
  Placement = pos=(142,-36,-67.4326) rot=(0.57735,0.57735,0.57735;2.0944rad)
FEATURE [App::Link] corner_bracket_40x042  label="corner_bracket_40x40_002"
  LinkPlacement = pos=(262,-587.433,56) rot=(0,1,0;1.5708rad)
  LinkedObject = -> <external ../parts_library/corner_bracket_40x40.FCStd>#Part__Feature
  Placement = pos=(262,-587.433,56) rot=(0,1,0;1.5708rad)
FEATURE [App::Link] corner_bracket_40x043  label="corner_bracket_40x40_003"
  LinkPlacement = pos=(262,-36,67.4326) rot=(0.57735,0.57735,-0.57735;4.18879rad)
  LinkedObject = -> <external ../parts_library/corner_bracket_40x40.FCStd>#Part__Feature
  Placement = pos=(262,-36,67.4326) rot=(0.57735,0.57735,-0.57735;4.18879rad)
FEATURE [App::FeaturePython] Joint011  label="Fixed_profile_40x40x500_right"  # Assembly joint (typed FeaturePython)
  Activated = true
  AngleMax = 0
  AngleMin = 0
  Detach1 = false
  Detach2 = false
  Distance = 0
  Distance2 = 0
  EnableAngleMax = false
  EnableAngleMin = false
  EnableLengthMax = false
  EnableLengthMin = false
  JointType = 0 (Fixed)
  LengthMax = 0
  LengthMin = 0
  Offset1 = pos=(262,0,0) rot=(0,0,1;0rad)
  Placement1 = pos=(262,-500,-1.137e-13) rot=(1,0,0;1.5708rad)
  Placement2 = pos=(0,0,350) rot=(0,-1,0;3.14159rad)
  Reference1 = -> Assembly [linear_shaft_25x501.Edge3,linear_shaft_25x501.Edge3]
  Reference2 = -> Assembly [profile_40x40x500.Edge292,profile_40x40x500.Edge292]
FEATURE [App::FeaturePython] Joint012  label="Fixed_corner_bracket_40x40_000"  # Assembly joint (typed FeaturePython)
  Activated = true
  AngleMax = 0
  AngleMin = 0
  Detach1 = false
  Detach2 = false
  Distance = 0
  Distance2 = 0
  EnableAngleMax = false
  EnableAngleMin = false
  EnableLengthMax = false
  EnableLengthMin = false
  JointType = 0 (Fixed)
  LengthMax = 0
  LengthMin = 0
  Offset1 = pos=(-2,0,0) rot=(0,0,1;0rad)
  Offset2 = pos=(0,0,-1) rot=(0,0,1;3.14159rad)
  Placement1 = pos=(-18,-20,350) rot=(0,0,1;0rad)
  Placement2 = pos=(36,87.4326,18) rot=(0.57735,-0.57735,-0.57735;4.18879rad)
  Reference1 = -> Assembly [profile_40x40x501.Edge386,profile_40x40x501.Vertex175]
  Reference2 = -> Assembly [corner_bracket_40x40.Edge44,corner_bracket_40x40.Vertex43]
FEATURE [App::FeaturePython] Joint013  label="Fixed_corner_bracket_40x40_001"  # Assembly joint (typed FeaturePython)
  Activated = true
  AngleMax = 0
  AngleMin = 0
  Detach1 = false
  Detach2 = false
  Distance = 0
  Distance2 = 0
  EnableAngleMax = false
  EnableAngleMin = false
  EnableLengthMax = false
  EnableLengthMin = false
  JointType = 0 (Fixed)
  LengthMax = 0
  LengthMin = 0
  Offset1 = pos=(-2,0,0) rot=(0,0,1;0rad)
  Offset2 = pos=(0,0,1) rot=(0,0,1;3.14159rad)
  Placement1 = pos=(-18,-20,-150) rot=(0,0,1;0rad)
  Placement2 = pos=(36,87.4326,18) rot=(0,-1,0;4.71239rad)
  Reference1 = -> Assembly [profile_40x40x501.Edge386,profile_40x40x501.Vertex89]
  Reference2 = -> Assembly [corner_bracket_40x041.Edge7,corner_bracket_40x041.Vertex7]
FEATURE [App::FeaturePython] Joint014  label="Fixed_corner_bracket_40x40_002"  # Assembly joint (typed FeaturePython)
  Activated = true
  AngleMax = 0
  AngleMin = 0
  Detach1 = false
  Detach2 = false
  Distance = 0
  Distance2 = 0
  EnableAngleMax = false
  EnableAngleMin = false
  EnableLengthMax = false
  EnableLengthMin = false
  JointType = 0 (Fixed)
  LengthMax = 0
  LengthMin = 0
  Offset1 = pos=(-2,0,0) rot=(0,0,1;0rad)
  Offset2 = pos=(0,0,-1) rot=(0,0,1;3.14159rad)
  Placement1 = pos=(-18,-20,350) rot=(0,0,1;0rad)
  Placement2 = pos=(36,87.4326,18) rot=(0.57735,-0.57735,-0.57735;4.18879rad)
  Reference1 = -> Assembly [profile_40x40x500.Edge386,profile_40x40x500.Vertex175]
  Reference2 = -> Assembly [corner_bracket_40x042.Edge44,corner_bracket_40x042.Vertex43]
FEATURE [App::FeaturePython] Joint015  label="Fixed_corner_bracket_40x40_003"  # Assembly joint (typed FeaturePython)
  Activated = true
  AngleMax = 0
  AngleMin = 0
  Detach1 = false
  Detach2 = false
  Distance = 0
  Distance2 = 0
  EnableAngleMax = false
  EnableAngleMin = false
  EnableLengthMax = false
  EnableLengthMin = false
  JointType = 0 (Fixed)
  LengthMax = 0
  LengthMin = 0
  Offset1 = pos=(-2,0,0) rot=(0,0,1;0rad)
  Offset2 = pos=(0,0,1) rot=(0,0,1;0rad)
  Placement1 = pos=(35,87.4326,16) rot=(0.707107,0,0.707107;3.14159rad)
  Placement2 = pos=(16,20,-149) rot=(0,0,1;0rad)
  Reference1 = -> Assembly [corner_bracket_40x043.Edge7,corner_bracket_40x043.Vertex7]
  Reference2 = -> Assembly [profile_40x40x500.Edge310,profile_40x40x500.Vertex33]
FEATURE [App::Link] surge_motor_mount_side
  LinkPlacement = pos=(202.065,-333.4,-0.05) rot=(0,0,1;3.14159rad)
  LinkedObject = -> <external surge_motor_mount_side.FCStd>#Body
  Placement = pos=(202.065,-333.4,-0.05) rot=(0,0,1;3.14159rad)
FEATURE [App::FeaturePython] Joint017  label="Fixed_surge_motor_mount_side"  # Assembly joint (typed FeaturePython)
  Activated = true
  AngleMax = 0
  AngleMin = 0
  Detach1 = false
  Detach2 = false
  Distance = 0
  Distance2 = 0
  EnableAngleMax = false
  EnableAngleMin = false
  EnableLengthMax = false
  EnableLengthMin = false
  JointType = 0 (Fixed)
  LengthMax = 0
  LengthMin = 0
  Placement1 = pos=(31.815,-31.7,8) rot=(0,0,1;3.14159rad)
  Placement2 = pos=(-31.75,0,36.25) rot=(1,0,0;1.5708rad)
  Reference1 = -> Assembly [_0ST_M02438.Part__Feature003.Edge45,_0ST_M02438.Part__Feature003.Edge45]
  Reference2 = -> Assembly [surge_motor_mount_side.Edge34,surge_motor_mount_side.Edge34]
FEATURE [App::Link] surge_motor_mount_bottom
  LinkPlacement = pos=(202,-410,1.7302e-12) rot=(0,0,1;0rad)
  LinkedObject = -> <external surge_motor_mount_bottom.FCStd>#Body
  Placement = pos=(202,-410,1.7302e-12) rot=(0,0,1;0rad)
FEATURE [App::FeaturePython] Joint018  label="Fixed_surge_motor_mount_bottom"  # Assembly joint (typed FeaturePython)
  Activated = true
  AngleMax = 0
  AngleMin = 0
  Detach1 = false
  Detach2 = false
  Distance = 0
  Distance2 = 0
  EnableAngleMax = false
  EnableAngleMin = false
  EnableLengthMax = false
  EnableLengthMin = false
  JointType = 0 (Fixed)
  LengthMax = 0
  LengthMin = 0
  Offset1 = pos=(0.4,13,0) rot=(0,0,1;0rad)
  Offset2 = pos=(0,0,0) rot=(0,0,1;1.5708rad)
  Placement1 = pos=(0,-38,-35.5) rot=(0.707107,0,0.707107;3.14159rad)
  Placement2 = pos=(1.95e-14,40,-106.6) rot=(-0.57735,0.57735,0.57735;4.18879rad)
  Reference1 = -> Assembly [surge_motor_mount_bottom.Edge46,surge_motor_mount_bottom.Edge46]
  Reference2 = -> Assembly [_0ST_M02438.Part__Feature006.Edge472,_0ST_M02438.Part__Feature006.Edge472]
FEATURE [App::Link] surge_motor_mount_top
  LinkPlacement = pos=(202,-410,1.7124e-12) rot=(0,0,1;0rad)
  LinkedObject = -> <external surge_motor_mount_top.FCStd>#Body
  Placement = pos=(202,-410,1.7124e-12) rot=(0,0,1;0rad)
FEATURE [App::FeaturePython] Joint019  label="Fixed_surge_motor_mount_top"  # Assembly joint (typed FeaturePython)
  Activated = true
  AngleMax = 0
  AngleMin = 0
  Detach1 = false
  Detach2 = false
  Distance = 0
  Distance2 = 0
  EnableAngleMax = false
  EnableAngleMin = false
  EnableLengthMax = false
  EnableLengthMin = false
  JointType = 0 (Fixed)
  LengthMax = 0
  LengthMin = 0
  Offset1 = pos=(-0.4,13,0) rot=(0,0,1;0rad)
  Offset2 = pos=(0,0,0) rot=(0,0,1;1.5708rad)
  Placement1 = pos=(0,-38,44.5) rot=(0.707107,0,0.707107;3.14159rad)
  Placement2 = pos=(2.629e-13,-40,-106.6) rot=(0.57735,-0.57735,0.57735;4.18879rad)
  Reference1 = -> Assembly [surge_motor_mount_top.Edge46,surge_motor_mount_top.Edge46]
  Reference2 = -> Assembly [_0ST_M02438.Part__Feature006.Edge167,_0ST_M02438.Part__Feature006.Edge167]
FEATURE [App::Link] surge_BK12_mount_bottom
  LinkPlacement = pos=(202,-223.15,4.92877e-10) rot=(0,0,1;0rad)
  LinkedObject = -> <external surge_BK12_mount_bottom.FCStd>#Body
  Placement = pos=(202,-223.15,4.92877e-10) rot=(0,0,1;0rad)
FEATURE [App::Link] surge_BK12_mount_top
  LinkPlacement = pos=(202,-223.15,4.92873e-10) rot=(0,0,1;0rad)
  LinkedObject = -> <external surge_BK12_mount_top.FCStd>#Body
  Placement = pos=(202,-223.15,4.92873e-10) rot=(0,0,1;0rad)
FEATURE [App::FeaturePython] Joint020  label="Fixed_surge_BK12_mount_top"  # Assembly joint (typed FeaturePython)
  Activated = true
  AngleMax = 0
  AngleMin = 0
  Detach1 = false
  Detach2 = false
  Distance = 0
  Distance2 = 0
  EnableAngleMax = false
  EnableAngleMin = false
  EnableLengthMax = false
  EnableLengthMin = false
  JointType = 0 (Fixed)
  LengthMax = 0
  LengthMin = 0
  Offset2 = pos=(0,0,-0.4) rot=(0,0,1;1.5708rad)
  Placement1 = pos=(23,6.5,32.5) rot=(0,0,-1;1.5708rad)
  Placement2 = pos=(23,-6,12) rot=(0,0,1;4.71239rad)
  Reference1 = -> Assembly [BK12.Part__Feature.Edge97,BK12.Part__Feature.Edge97]
  Reference2 = -> Assembly [surge_BK12_mount_top.Edge61,surge_BK12_mount_top.Edge61]
FEATURE [App::FeaturePython] Joint021  label="Fixed_surge_BK12_mount_bottom"  # Assembly joint (typed FeaturePython)
  Activated = true
  AngleMax = 0
  AngleMin = 0
  Detach1 = false
  Detach2 = false
  Distance = 0
  Distance2 = 0
  EnableAngleMax = false
  EnableAngleMin = false
  EnableLengthMax = false
  EnableLengthMin = false
  JointType = 0 (Fixed)
  LengthMax = 0
  LengthMin = 0
  Offset2 = pos=(0,0,-0.4) rot=(0,0,-1;1.5708rad)
  Placement1 = pos=(23,-6,-20.9) rot=(0,0,1;3.14159rad)
  Placement2 = pos=(23,6.5,-0.4) rot=(0,0,-1;3.14159rad)
  Reference1 = -> Assembly [surge_BK12_mount_bottom.Edge59,surge_BK12_mount_bottom.Edge59]
  Reference2 = -> Assembly [BK12.Part__Feature.Face28,BK12.Part__Feature.Edge11]
FEATURE [Assembly::JointGroup] Joints
  Group = -> [GroundedJoint,Joint,Joint001,Joint002,Joint003,Joint004,Joint005,Joint006,Joint008,Joint009,Joint010,Joint011,Joint012,Joint013,Joint014,Joint015,Joint017,Joint018,Joint019,Joint020,Joint021]
FEATURE [Assembly::AssemblyObject] Assembly  label="surge_platform"
  Group = -> [Joints,linear_shaft_25x500,linear_shaft_25x501,GroundedJoint,Joint,SHF25,SHF026,SHF027,SHF028,Joint001,Joint002,Joint003,Joint004,_0ST_M02438,Joint005,SFU1605_ball_screw_250mm,BK12,coupler_10x19,Joint006,Joint008,Joint009,profile_40x40x500,profile_40x40x501,corner_bracket_40x40,corner_bracket_40x041,corner_bracket_40x042,corner_bracket_40x043,Joint010,Joint011,Joint012,Joint013,Joint014,Joint015,+10 more]
  Origin = -> Origin
  Type = Assembly
---- part sway_platform.FCStd = doc fcstd_d49f6134f0a7 ----
FCSTD DOCUMENT  (FreeCAD 1.0R39109 (Git))
Label: sway_platform
License: All rights reserved
LicenseURL: https://en.wikipedia.org/wiki/All_rights_reserved
objects: App::Link×28, App::FeaturePython×28, Assembly::JointGroup×1, Assembly::AssemblyObject×1
EXTERNAL_REF file=../parts_library/SC25UU_to_SH25.FCStd obj=Body
EXTERNAL_REF file=../parts_library/SC25UU.FCStd obj=Part__Feature341
EXTERNAL_REF file=../parts_library/SH25.FCStd obj=Part__Feature337
EXTERNAL_REF file=../parts_library/linear_shaft.FCStd obj=Body001
EXTERNAL_REF file=../parts_library/DSG16H_to_SH25.FCStd obj=Body
EXTERNAL_REF file=../parts_library/SFU1605.FCStd obj=Part__Feature048
EXTERNAL_REF file=../parts_library/SFU1605.FCStd obj=Part__Feature047
EXTERNAL_REF file=../parts_library/motor.FCStd obj=SERVOMOTOR_80ST_M02430
EXTERNAL_REF file=../parts_library/coupler.FCStd obj=Body
EXTERNAL_REF file=../parts_library/SFU1605.FCStd obj=SFU1605_250_v6
EXTERNAL_REF file=../parts_library/SFU1605.FCStd obj=BK12_v3
EXTERNAL_REF file=sway_SC25UU_to_SH25_with_plate.FCStd obj=Body
EXTERNAL_REF file=sway_motor_mount_rear_plate.FCStd obj=Body
EXTERNAL_REF file=sway_motor_mount_front_plate.FCStd obj=Body
EXTERNAL_REF file=sway_motor_mount_front_plate_shaft_support.FCStd obj=Body
EXTERNAL_REF file=sway_motor_mount_side.FCStd obj=Body
EXTERNAL_REF file=sway_motor_mount_top.FCStd obj=Body
EXTERNAL_REF file=sway_motor_mount_bottom.FCStd obj=Body

FEATURE [App::Link] SC25UU_to_SH25  label="SC25UU_to_SH25_000"
  LinkedObject = -> <external ../parts_library/SC25UU_to_SH25.FCStd>#Body
FEATURE [App::Link] SC25UU_to_SH026  label="SC25UU_to_SH25_001"
  LinkPlacement = pos=(1e-15,204,-1e-16) rot=(0,0,1;0rad)
  LinkedObject = -> <external ../parts_library/SC25UU_to_SH25.FCStd>#Body
  Placement = pos=(1e-15,204,-1e-16) rot=(0,0,1;0rad)
FEATURE [App::FeaturePython] GroundedJoint  label="GroundedJoint_SC25UU_to_SH25_000"  # Assembly grounded joint (typed FeaturePython)
  ObjectToGround = -> SC25UU_to_SH25
FEATURE [App::FeaturePython] Joint  label="Fixed_SC25UU_to_SH25_001"  # Assembly joint (typed FeaturePython)
  Activated = true
  AngleMax = 0
  AngleMin = 0
  Detach1 = false
  Detach2 = false
  Distance = 0
  Distance2 = 0
  EnableAngleMax = false
  EnableAngleMin = false
  EnableLengthMax = false
  EnableLengthMin = false
  JointType = 0 (Fixed)
  LengthMax = 0
  LengthMin = 0
  Offset2 = pos=(0,0,-204) rot=(0,0,1;0rad)
  Placement1 = pos=(38,-1.5,5) rot=(-1,0,0;1.5708rad)
  Placement2 = pos=(38,-205.5,5) rot=(-1,0,0;1.5708rad)
  Reference1 = -> Assembly [SC25UU_to_SH25.Face9,SC25UU_to_SH25.Face9]
  Reference2 = -> Assembly [SC25UU_to_SH026.Face9,SC25UU_to_SH026.Face9]
FEATURE [App::Link] SC25UU  label="SC25UU_000"
  LinkPlacement = pos=(38,67,-415.5) rot=(1,0,0;1.5708rad)
  LinkedObject = -> <external ../parts_library/SC25UU.FCStd>#Part__Feature341
  Placement = pos=(38,67,-415.5) rot=(1,0,0;1.5708rad)
FEATURE [App::Link] SC25UU001  label="SC25UU_001"
  LinkPlacement = pos=(38,271,-415.5) rot=(1,0,0;1.5708rad)
  LinkedObject = -> <external ../parts_library/SC25UU.FCStd>#Part__Feature341
  Placement = pos=(38,271,-415.5) rot=(1,0,0;1.5708rad)
FEATURE [App::Link] SC25UU002  label="SC25UU_002"
  LinkPlacement = pos=(442,67,-415.5) rot=(1,0,0;1.5708rad)
  LinkedObject = -> <external ../parts_library/SC25UU.FCStd>#Part__Feature341
  Placement = pos=(442,67,-415.5) rot=(1,0,0;1.5708rad)
FEATURE [App::Link] SC25UU003  label="SC25UU_003"
  LinkPlacement = pos=(442,271,-415.5) rot=(1,0,0;1.5708rad)
  LinkedObject = -> <external ../parts_library/SC25UU.FCStd>#Part__Feature341
  Placement = pos=(442,271,-415.5) rot=(1,0,0;1.5708rad)
FEATURE [App::FeaturePython] Joint003  label="Fixed_SC25UU_000"  # Assembly joint (typed FeaturePython)
  Activated = true
  AngleMax = 0
  AngleMin = 0
  Detach1 = false
  Detach2 = false
  Distance = 0
  Distance2 = 0
  EnableAngleMax = false
  EnableAngleMin = false
  EnableLengthMax = false
  EnableLengthMin = false
  JointType = 0 (Fixed)
  LengthMax = 0
  LengthMin = 0
  Offset2 = pos=(0,0,0) rot=(0,0,-1;1.5708rad)
  Placement1 = pos=(-27,415.5,58.5) rot=(0.57735,-0.57735,0.57735;2.0944rad)
  Placement2 = pos=(11,8.5,0) rot=(0,0,-1;1.5708rad)
  Reference1 = -> Assembly [SC25UU.Edge66,SC25UU.Edge66]
  Reference2 = -> Assembly [SC25UU_to_SH25.Edge16,SC25UU_to_SH25.Edge16]
FEATURE [App::FeaturePython] Joint004  label="Fixed_SC25UU_001"  # Assembly joint (typed FeaturePython)
  Activated = true
  AngleMax = 0
  AngleMin = 0
  Detach1 = false
  Detach2 = false
  Distance = 0
  Distance2 = 0
  EnableAngleMax = false
  EnableAngleMin = false
  EnableLengthMax = false
  EnableLengthMin = false
  JointType = 0 (Fixed)
  LengthMax = 0
  LengthMin = 0
  Offset2 = pos=(0,0,0) rot=(0,0,-1;1.5708rad)
  Placement1 = pos=(11,8.5,0) rot=(0,0,1;0rad)
  Placement2 = pos=(-27,415.5,58.5) rot=(1,0,0;1.5708rad)
  Reference1 = -> Assembly [SC25UU_to_SH026.Edge16,SC25UU_to_SH026.Edge16]
  Reference2 = -> Assembly [SC25UU001.Edge66,SC25UU001.Edge66]
FEATURE [App::Link] SH25  label="SH25_000"
  LinkPlacement = pos=(-901.062,343.027,-226.938) rot=(0,0,1;0rad)
  LinkedObject = -> <external ../parts_library/SH25.FCStd>#Part__Feature337
  Placement = pos=(-901.062,343.027,-226.938) rot=(0,0,1;0rad)
FEATURE [App::Link] SH026  label="SH25_001"
  LinkPlacement = pos=(977.062,-72.0272,-226.938) rot=(0,0,1;3.14159rad)
  LinkedObject = -> <external ../parts_library/SH25.FCStd>#Part__Feature337
  Placement = pos=(977.062,-72.0272,-226.938) rot=(0,0,1;3.14159rad)
FEATURE [App::Link] SH027  label="SH25_002"
  LinkPlacement = pos=(-497.062,343.027,-226.938) rot=(0,0,1;0rad)
  LinkedObject = -> <external ../parts_library/SH25.FCStd>#Part__Feature337
  Placement = pos=(-497.062,343.027,-226.938) rot=(0,0,1;0rad)
FEATURE [App::Link] SH028  label="SH25_003"
  LinkPlacement = pos=(1381.06,-72.0272,-226.938) rot=(0,0,1;3.14159rad)
  LinkedObject = -> <external ../parts_library/SH25.FCStd>#Part__Feature337
  Placement = pos=(1381.06,-72.0272,-226.938) rot=(0,0,1;3.14159rad)
FEATURE [App::FeaturePython] Joint007  label="Fixed_SH25_000"  # Assembly joint (typed FeaturePython)
  Activated = true
  AngleMax = 0
  AngleMin = 0
  Detach1 = false
  Detach2 = false
  Distance = 0
  Distance2 = 0
  EnableAngleMax = false
  EnableAngleMin = false
  EnableLengthMax = false
  EnableLengthMin = false
  JointType = 0 (Fixed)
  LengthMax = 0
  LengthMin = 0
  Offset2 = pos=(0,0,0) rot=(0,0,1;3.14159rad)
  Placement1 = pos=(38,5.5,10) rot=(0,0,1;0rad)
  Placement2 = pos=(939.062,-337.527,236.938) rot=(0,0,1;0rad)
  Reference1 = -> Assembly [SC25UU_to_SH25.Edge46,SC25UU_to_SH25.Edge46]
  Reference2 = -> Assembly [SH25.Edge16,SH25.Edge16]
FEATURE [App::FeaturePython] Joint008  label="Fixed_SH25_001"  # Assembly joint (typed FeaturePython)
  Activated = true
  AngleMax = 0
  AngleMin = 0
  Detach1 = false
  Detach2 = false
  Distance = 0
  Distance2 = 0
  EnableAngleMax = false
  EnableAngleMin = false
  EnableLengthMax = false
  EnableLengthMin = false
  JointType = 0 (Fixed)
  LengthMax = 0
  LengthMin = 0
  Placement1 = pos=(939.062,-337.527,236.938) rot=(0,0,-1;3.14159rad)
  Placement2 = pos=(38,61.5,10) rot=(0,0,1;0rad)
  Reference1 = -> Assembly [SH026.Edge16,SH026.Edge16]
  Reference2 = -> Assembly [SC25UU_to_SH026.Edge49,SC25UU_to_SH026.Edge49]
FEATURE [App::Link] linear_shaft_25x428  label="linear_shaft_25x428_front"
  LinkPlacement = pos=(454,33.5,45) rot=(0,0,-1;1.5708rad)
  LinkedObject = -> <external ../parts_library/linear_shaft.FCStd>#Body001
  Placement = pos=(454,33.5,45) rot=(0,0,-1;1.5708rad)
FEATURE [App::Link] linear_shaft_25x429  label="linear_shaft_25x428_rear"
  LinkPlacement = pos=(454,237.5,45) rot=(0.707107,0.707107,0;3.14159rad)
  LinkedObject = -> <external ../parts_library/linear_shaft.FCStd>#Body001
  Placement = pos=(454,237.5,45) rot=(0.707107,0.707107,0;3.14159rad)
FEATURE [App::FeaturePython] Joint011  label="Fixed_linear_shaft_25x428_front"  # Assembly joint (typed FeaturePython)
  Activated = true
  AngleMax = 0
  AngleMin = 0
  Detach1 = false
  Detach2 = false
  Distance = 0
  Distance2 = 0
  EnableAngleMax = false
  EnableAngleMin = false
  EnableLengthMax = false
  EnableLengthMin = false
  JointType = 0 (Fixed)
  LengthMax = 0
  LengthMin = 0
  Placement1 = pos=(-7.1e-15,-428,-1.421e-13) rot=(-1,0,0;4.71239rad)
  Placement2 = pos=(927.062,-309.527,271.938) rot=(-0.57735,0.57735,-0.57735;2.0944rad)
  Reference1 = -> Assembly [linear_shaft_25x428.Edge3,linear_shaft_25x428.Edge3]
  Reference2 = -> Assembly [SH25.Edge18,SH25.Edge18]
FEATURE [App::FeaturePython] Joint012  label="Fixed_linear_shaft_25x428_rear"  # Assembly joint (typed FeaturePython)
  Activated = true
  AngleMax = 0
  AngleMin = 0
  Detach1 = false
  Detach2 = false
  Distance = 0
  Distance2 = 0
  EnableAngleMax = false
  EnableAngleMin = false
  EnableLengthMax = false
  EnableLengthMin = false
  JointType = 0 (Fixed)
  LengthMax = 0
  LengthMin = 0
  Placement1 = pos=(0,-428,-1.137e-13) rot=(-1,0,0;4.71239rad)
  Placement2 = pos=(951.062,-309.527,271.938) rot=(-0.57735,0.57735,-0.57735;2.0944rad)
  Reference1 = -> Assembly [linear_shaft_25x429.Edge3,linear_shaft_25x429.Edge3]
  Reference2 = -> Assembly [SH026.Edge26,SH026.Edge26]
FEATURE [App::Link] SH029  label="SH25_004"
  LinkPlacement = pos=(1179.06,-72.0272,-226.938) rot=(0,0,1;3.14159rad)
  LinkedObject = -> <external ../parts_library/SH25.FCStd>#Part__Feature337
  Placement = pos=(1179.06,-72.0272,-226.938) rot=(0,0,1;3.14159rad)
FEATURE [App::FeaturePython] Joint013  label="Fixed_SH25_004"  # Assembly joint (typed FeaturePython)
  Activated = true
  AngleMax = 0
  AngleMin = 0
  Detach1 = false
  Detach2 = false
  Distance = 0
  Distance2 = 0
  EnableAngleMax = false
  EnableAngleMin = false
  EnableLengthMax = false
  EnableLengthMin = false
  JointType = 0 (Fixed)
  LengthMax = 0
  LengthMin = 0
  Offset2 = pos=(0,0,202) rot=(0,0,1;0rad)
  Placement1 = pos=(0,-428,-1.137e-13) rot=(-1,0,0;4.71239rad)
  Placement2 = pos=(1153.06,-309.527,271.938) rot=(-0.57735,0.57735,-0.57735;2.0944rad)
  Reference1 = -> Assembly [linear_shaft_25x429.Edge3,linear_shaft_25x429.Edge3]
  Reference2 = -> Assembly [SH029.Edge26,SH029.Edge26]
FEATURE [App::Link] DSG16H_to_SH25
  LinkPlacement = pos=(215,218.5,-2) rot=(0,0,1;0rad)
  LinkedObject = -> <external ../parts_library/DSG16H_to_SH25.FCStd>#Body
  Placement = pos=(215,218.5,-2) rot=(0,0,1;0rad)
FEATURE [App::FeaturePython] Joint014  label="Fixed_DSG16H_to_SH25"  # Assembly joint (typed FeaturePython)
  Activated = true
  AngleMax = 0
  AngleMin = 0
  Detach1 = false
  Detach2 = false
  Distance = 0
  Distance2 = 0
  EnableAngleMax = false
  EnableAngleMin = false
  EnableLengthMax = false
  EnableLengthMin = false
  JointType = 0 (Fixed)
  LengthMax = 0
  LengthMin = 0
  Placement1 = pos=(25,-9,12) rot=(0,0,1;0rad)
  Placement2 = pos=(939.062,-281.527,236.938) rot=(0,0,-1;3.14159rad)
  Reference1 = -> Assembly [DSG16H_to_SH25.Edge103,DSG16H_to_SH25.Edge103]
  Reference2 = -> Assembly [SH029.Edge8,SH029.Edge8]
FEATURE [App::Link] DSG16H
  LinkPlacement = pos=(240,217.5,-22) rot=(0,0,1;0rad)
  LinkedObject = -> <external ../parts_library/SFU1605.FCStd>#Part__Feature048
  Placement = pos=(240,217.5,-22) rot=(0,0,1;0rad)
FEATURE [App::FeaturePython] Joint015  label="Fixed_DSG16H"  # Assembly joint (typed FeaturePython)
  Activated = true
  AngleMax = 0
  AngleMin = 0
  Detach1 = false
  Detach2 = false
  Distance = 0
  Distance2 = 0
  EnableAngleMax = false
  EnableAngleMin = false
  EnableLengthMax = false
  EnableLengthMin = false
  JointType = 0 (Fixed)
  LengthMax = 0
  LengthMin = 0
  Offset2 = pos=(0,0,0) rot=(0,0,1;3.14159rad)
  Placement1 = pos=(-20,8,20) rot=(0,0,1;3.14159rad)
  Placement2 = pos=(5,7,0) rot=(0,0,1;3.14159rad)
  Reference1 = -> Assembly [DSG16H.Edge1307,DSG16H.Edge1307]
  Reference2 = -> Assembly [DSG16H_to_SH25.Edge20,DSG16H_to_SH25.Edge20]
FEATURE [App::Link] SFU1605_ball_screw_nut
  LinkPlacement = pos=(240,207.25,-22) rot=(0,-1,0;1.5708rad)
  LinkedObject = -> <external ../parts_library/SFU1605.FCStd>#Part__Feature047
  Placement = pos=(240,207.25,-22) rot=(0,-1,0;1.5708rad)
FEATURE [App::FeaturePython] Joint016  label="Fixed_SFU1605_ball_screw_nut"  # Assembly joint (typed FeaturePython)
  Activated = true
  AngleMax = 0
  AngleMin = 0
  Detach1 = false
  Detach2 = false
  Distance = 0
  Distance2 = 0
  EnableAngleMax = false
  EnableAngleMin = false
  EnableLengthMax = false
  EnableLengthMin = false
  JointType = 0 (Fixed)
  LengthMax = 0
  LengthMin = 0
  Placement1 = pos=(0,20,0) rot=(-1,0,0;1.5708rad)
  Placement2 = pos=(7.1e-15,30.25,0) rot=(0.57735,0.57735,-0.57735;2.0944rad)
  Reference1 = -> Assembly [DSG16H.Face478,DSG16H.Face478]
  Reference2 = -> Assembly [SFU1605_ball_screw_nut.Face46,SFU1605_ball_screw_nut.Face46]
FEATURE [App::Link] _0ST_M02438  label="80ST-M02438"
  LinkPlacement = pos=(342.4,135.5,30) rot=(0.57735,-0.57735,-0.57735;2.0944rad)
  LinkedObject = -> <external ../parts_library/motor.FCStd>#SERVOMOTOR_80ST_M02430
  Placement = pos=(342.4,135.5,30) rot=(0.57735,-0.57735,-0.57735;2.0944rad)
FEATURE [App::FeaturePython] Joint017  label="Fixed_80ST-M02438"  # Assembly joint (typed FeaturePython)
  Activated = true
  AngleMax = 0
  AngleMin = 0
  Detach1 = false
  Detach2 = false
  Distance = 0
  Distance2 = 0
  EnableAngleMax = false
  EnableAngleMin = false
  EnableLengthMax = false
  EnableLengthMin = false
  JointType = 0 (Fixed)
  LengthMax = 0
  LengthMin = 0
  Offset1 = pos=(-102,15,0) rot=(0,0,1;0rad)
  Offset2 = pos=(0,0,-31) rot=(0,0,1;0rad)
  Placement1 = pos=(-102,3e-15,15) rot=(-1,0,0;4.71239rad)
  Placement2 = pos=(0,0,-111.6) rot=(0,1,0;3.14159rad)
  Reference1 = -> Assembly [linear_shaft_25x429.Edge2,linear_shaft_25x429.Edge2]
  Reference2 = -> Assembly [_0ST_M02438.Part__Feature004.Edge14,_0ST_M02438.Part__Feature004.Edge14]
FEATURE [App::Link] coupler_10x19
  LinkPlacement = pos=(266.25,135.5,30) rot=(-0.57735,0.57735,0.57735;2.0944rad)
  LinkedObject = -> <external ../parts_library/coupler.FCStd>#Body
  Placement = pos=(266.25,135.5,30) rot=(-0.57735,0.57735,0.57735;2.0944rad)
FEATURE [App::FeaturePython] Joint018  label="Fixed_coupler_10x19"  # Assembly joint (typed FeaturePython)
  Activated = true
  AngleMax = 0
  AngleMin = 0
  Detach1 = false
  Detach2 = false
  Distance = 0
  Distance2 = 0
  EnableAngleMax = false
  EnableAngleMin = false
  EnableLengthMax = false
  EnableLengthMin = false
  JointType = 0 (Fixed)
  LengthMax = 0
  LengthMin = 0
  Offset2 = pos=(0,0,1.65) rot=(0,0,1;0rad)
  Placement1 = pos=(0,0,43) rot=(0,0,1;0rad)
  Placement2 = pos=(3.7e-15,-33.15,-7e-16) rot=(1,0,0;1.5708rad)
  Reference1 = -> Assembly [_0ST_M02438.Part__Feature002.Edge5,_0ST_M02438.Part__Feature002.Edge5]
  Reference2 = -> Assembly [coupler_10x19.Edge9,coupler_10x19.Edge9]
FEATURE [App::Link] SFU1605_ball_screw_250mm
  LinkPlacement = pos=(497.25,135.5,30) rot=(0.57735,0.57735,0.57735;2.0944rad)
  LinkedObject = -> <external ../parts_library/SFU1605.FCStd>#SFU1605_250_v6
  Placement = pos=(497.25,135.5,30) rot=(0.57735,0.57735,0.57735;2.0944rad)
FEATURE [App::FeaturePython] Joint019  label="Fixed_SFU1605_ball_screw_250mm"  # Assembly joint (typed FeaturePython)
  Activated = true
  AngleMax = 0
  AngleMin = 0
  Detach1 = false
  Detach2 = false
  Distance = 0
  Distance2 = 0
  EnableAngleMax = false
  EnableAngleMin = false
  EnableLengthMax = false
  EnableLengthMin = false
  JointType = 0 (Fixed)
  LengthMax = 0
  LengthMin = 0
  Offset2 = pos=(0,0,4) rot=(0,0,1;0rad)
  Placement1 = pos=(2e-16,3e-16,0) rot=(0,0,1;0rad)
  Placement2 = pos=(3.1e-15,-14.5,1.8e-15) rot=(-1,0,0;1.5708rad)
  Reference1 = -> Assembly [SFU1605_ball_screw_250mm.Part__Feature110.Edge105,SFU1605_ball_screw_250mm.Part__Feature110.Edge105]
  Reference2 = -> Assembly [coupler_10x19.Edge7,coupler_10x19.Edge7]
FEATURE [App::Link] BK12
  LinkPlacement = pos=(240,135.5,55) rot=(0.707107,-0.707107,0;3.14159rad)
  LinkedObject = -> <external ../parts_library/SFU1605.FCStd>#BK12_v3
  Placement = pos=(240,135.5,55) rot=(0.707107,-0.707107,0;3.14159rad)
FEATURE [App::FeaturePython] Joint020  label="Fixed_BK12"  # Assembly joint (typed FeaturePython)
  Activated = true
  AngleMax = 0
  AngleMin = 0
  Detach1 = false
  Detach2 = false
  Distance = 0
  Distance2 = 0
  EnableAngleMax = false
  EnableAngleMin = false
  EnableLengthMax = false
  EnableLengthMin = false
  JointType = 0 (Fixed)
  LengthMax = 0
  LengthMin = 0
  Placement1 = pos=(2e-16,3e-16,-53.75) rot=(0,0,1;0rad)
  Placement2 = pos=(1.1e-15,13,25) rot=(0,0.707107,0.707107;3.14159rad)
  Reference1 = -> Assembly [SFU1605_ball_screw_250mm.Part__Feature110.Edge52,SFU1605_ball_screw_250mm.Part__Feature110.Edge52]
  Reference2 = -> Assembly [BK12.Part__Feature030.Edge19,BK12.Part__Feature030.Edge19]
FEATURE [App::Link] sway_SC25UU_to_SH25_with_plate  label="sway_SC25UU_to_SH25_with_plate_001"
  LinkPlacement = pos=(404,204,3e-16) rot=(0,0,1;0rad)
  LinkedObject = -> <external sway_SC25UU_to_SH25_with_plate.FCStd>#Body
  Placement = pos=(404,204,3e-16) rot=(0,0,1;0rad)
FEATURE [App::FeaturePython] Joint022  label="Fixed_SC25UU_003"  # Assembly joint (typed FeaturePython)
  Activated = true
  AngleMax = 0
  AngleMin = 0
  Detach1 = false
  Detach2 = false
  Distance = 0
  Distance2 = 0
  EnableAngleMax = false
  EnableAngleMin = false
  EnableLengthMax = false
  EnableLengthMin = false
  JointType = 0 (Fixed)
  LengthMax = 0
  LengthMin = 0
  Offset2 = pos=(0,0,0) rot=(0,0,-1;1.5708rad)
  Placement1 = pos=(65,58.5,0) rot=(0,0,1;0rad)
  Placement2 = pos=(27,415.5,8.5) rot=(1,0,0;1.5708rad)
  Reference1 = -> Assembly [sway_SC25UU_to_SH25_with_plate.Edge31,sway_SC25UU_to_SH25_with_plate.Edge31]
  Reference2 = -> Assembly [SC25UU003.Edge29,SC25UU003.Edge29]
FEATURE [App::FeaturePython] Joint023  label="Fixed_SH25_003"  # Assembly joint (typed FeaturePython)
  Activated = true
  AngleMax = 0
  AngleMin = 0
  Detach1 = false
  Detach2 = false
  Distance = 0
  Distance2 = 0
  EnableAngleMax = false
  EnableAngleMin = false
  EnableLengthMax = false
  EnableLengthMin = false
  JointType = 0 (Fixed)
  LengthMax = 0
  LengthMin = 0
  Placement1 = pos=(38,61.5,10) rot=(0,0,1;0rad)
  Placement2 = pos=(939.062,-337.527,236.938) rot=(0,0,-1;3.14159rad)
  Reference1 = -> Assembly [sway_SC25UU_to_SH25_with_plate.Edge90,sway_SC25UU_to_SH25_with_plate.Edge90]
  Reference2 = -> Assembly [SH028.Edge16,SH028.Edge16]
FEATURE [App::Link] sway_motor_mount_rear_plate
  LinkPlacement = pos=(430,272.5,5) rot=(0,0,1;3.14159rad)
  LinkedObject = -> <external sway_motor_mount_rear_plate.FCStd>#Body
  Placement = pos=(430,272.5,5) rot=(0,0,1;3.14159rad)
FEATURE [App::FeaturePython] Joint024  label="Fixed_sway_motor_mount_rear_plate"  # Assembly joint (typed FeaturePython)
  Activated = true
  AngleMax = 0
  AngleMin = 0
  Detach1 = false
  Detach2 = false
  Distance = 0
  Distance2 = 0
  EnableAngleMax = false
  EnableAngleMin = false
  EnableLengthMax = false
  EnableLengthMin = false
  JointType = 0 (Fixed)
  LengthMax = 0
  LengthMin = 0
  Offset2 = pos=(0,0,0) rot=(0,0,1;3.14159rad)
  Placement1 = pos=(11,58.5,5) rot=(1,0,0;3.14159rad)
  Placement2 = pos=(15,10,0) rot=(0,0,1;3.14159rad)
  Reference1 = -> Assembly [sway_SC25UU_to_SH25_with_plate.Edge39,sway_SC25UU_to_SH25_with_plate.Edge39]
  Reference2 = -> Assembly [sway_motor_mount_rear_plate.Edge10,sway_motor_mount_rear_plate.Edge10]
FEATURE [App::Link] sway_SC25UU_to_SH25_with_plate001  label="sway_SC25UU_to_SH25_with_plate_000"
  LinkPlacement = pos=(404,-1e-16,3e-16) rot=(0,0,1;0rad)
  LinkedObject = -> <external sway_SC25UU_to_SH25_with_plate.FCStd>#Body
  Placement = pos=(404,-1e-16,3e-16) rot=(0,0,1;0rad)
FEATURE [App::FeaturePython] Joint025  label="Fixed_sway_SC25UU_to_SH25_with_plate_000"  # Assembly joint (typed FeaturePython)
  Activated = true
  AngleMax = 0
  AngleMin = 0
  Detach1 = false
  Detach2 = false
  Distance = 0
  Distance2 = 0
  EnableAngleMax = false
  EnableAngleMin = false
  EnableLengthMax = false
  EnableLengthMin = false
  JointType = 0 (Fixed)
  LengthMax = 0
  LengthMin = 0
  Offset1 = pos=(-404,0,0) rot=(0,0,1;0rad)
  Placement1 = pos=(-366,-1.5,5) rot=(-1,0,0;1.5708rad)
  Placement2 = pos=(38,-1.5,5) rot=(-1,0,0;1.5708rad)
  Reference1 = -> Assembly [sway_SC25UU_to_SH25_with_plate001.Face9,sway_SC25UU_to_SH25_with_plate001.Face9]
  Reference2 = -> Assembly [SC25UU_to_SH25.Face9,SC25UU_to_SH25.Face9]
FEATURE [App::FeaturePython] Joint026  label="Fixed_sway_SC25UU_to_SH25_with_plate_001"  # Assembly joint (typed FeaturePython)
  Activated = true
  AngleMax = 0
  AngleMin = 0
  Detach1 = false
  Detach2 = false
  Distance = 0
  Distance2 = 0
  EnableAngleMax = false
  EnableAngleMin = false
  EnableLengthMax = false
  EnableLengthMin = false
  JointType = 0 (Fixed)
  LengthMax = 0
  LengthMin = 0
  Offset2 = pos=(0,0,-204) rot=(0,0,1;0rad)
  Placement1 = pos=(38,-1.5,5) rot=(-1,0,0;1.5708rad)
  Placement2 = pos=(38,-205.5,5) rot=(-1,0,0;1.5708rad)
  Reference1 = -> Assembly [sway_SC25UU_to_SH25_with_plate001.Face9,sway_SC25UU_to_SH25_with_plate001.Face9]
  Reference2 = -> Assembly [sway_SC25UU_to_SH25_with_plate.Face9,sway_SC25UU_to_SH25_with_plate.Face9]
FEATURE [App::FeaturePython] Joint027  label="Fixed_SC25UU_002"  # Assembly joint (typed FeaturePython)
  Activated = true
  AngleMax = 0
  AngleMin = 0
  Detach1 = false
  Detach2 = false
  Distance = 0
  Distance2 = 0
  EnableAngleMax = false
  EnableAngleMin = false
  EnableLengthMax = false
  EnableLengthMin = false
  JointType = 0 (Fixed)
  LengthMax = 0
  LengthMin = 0
  Offset2 = pos=(0,0,0) rot=(0,0,-1;1.5708rad)
  Placement1 = pos=(27,415.5,8.5) rot=(0.57735,-0.57735,0.57735;2.0944rad)
  Placement2 = pos=(65,58.5,0) rot=(0,0,-1;1.5708rad)
  Reference1 = -> Assembly [SC25UU002.Edge29,SC25UU002.Edge29]
  Reference2 = -> Assembly [sway_SC25UU_to_SH25_with_plate001.Edge31,sway_SC25UU_to_SH25_with_plate001.Edge31]
FEATURE [App::FeaturePython] Joint028  label="Fixed_SH25_002"  # Assembly joint (typed FeaturePython)
  Activated = true
  AngleMax = 0
  AngleMin = 0
  Detach1 = false
  Detach2 = false
  Distance = 0
  Distance2 = 0
  EnableAngleMax = false
  EnableAngleMin = false
  EnableLengthMax = false
  EnableLengthMin = false
  JointType = 0 (Fixed)
  LengthMax = 0
  LengthMin = 0
  Offset2 = pos=(0,0,0) rot=(0,0,1;3.14159rad)
  Placement1 = pos=(38,61.5,10) rot=(0,0,1;0rad)
  Placement2 = pos=(939.062,-281.527,236.938) rot=(0,0,1;0rad)
  Reference1 = -> Assembly [sway_SC25UU_to_SH25_with_plate001.Edge90,sway_SC25UU_to_SH25_with_plate001.Edge90]
  Reference2 = -> Assembly [SH027.Edge8,SH027.Edge8]
FEATURE [App::Link] sway_motor_mount_front_plate
  LinkPlacement = pos=(430,68.5,5) rot=(0,0,1;3.14159rad)
  LinkedObject = -> <external sway_motor_mount_front_plate.FCStd>#Body
  Placement = pos=(430,68.5,5) rot=(0,0,1;3.14159rad)
FEATURE [App::FeaturePython] Joint029  label="Fixed_sway_motor_mount_front_plate"  # Assembly joint (typed FeaturePython)
  Activated = true
  AngleMax = 0
  AngleMin = 0
  Detach1 = false
  Detach2 = false
  Distance = 0
  Distance2 = 0
  EnableAngleMax = false
  EnableAngleMin = false
  EnableLengthMax = false
  EnableLengthMin = false
  JointType = 0 (Fixed)
  LengthMax = 0
  LengthMin = 0
  Offset2 = pos=(0,0,0) rot=(0,0,1;3.14159rad)
  Placement1 = pos=(11,58.5,5) rot=(1,0,0;3.14159rad)
  Placement2 = pos=(15,10,0) rot=(0,0,1;3.14159rad)
  Reference1 = -> Assembly [sway_SC25UU_to_SH25_with_plate001.Edge39,sway_SC25UU_to_SH25_with_plate001.Edge39]
  Reference2 = -> Assembly [sway_motor_mount_front_plate.Edge14,sway_motor_mount_front_plate.Edge14]
FEATURE [App::Link] sway_motor_mount_front_plate_shaft_support
  LinkPlacement = pos=(252,33.5,45) rot=(0,0,1;3.14159rad)
  LinkedObject = -> <external sway_motor_mount_front_plate_shaft_support.FCStd>#Body
  Placement = pos=(252,33.5,45) rot=(0,0,1;3.14159rad)
FEATURE [App::FeaturePython] Joint030  label="Fixed_sway_motor_mount_front_plate_shaft_support"  # Assembly joint (typed FeaturePython)
  Activated = true
  AngleMax = 0
  AngleMin = 0
  Detach1 = false
  Detach2 = false
  Distance = 0
  Distance2 = 0
  EnableAngleMax = false
  EnableAngleMin = false
  EnableLengthMax = false
  EnableLengthMin = false
  JointType = 0 (Fixed)
  LengthMax = 0
  LengthMin = 0
  Offset2 = pos=(0,0,-202) rot=(0,0,1;0rad)
  Placement1 = pos=(951.062,-309.527,271.938) rot=(-0.57735,0.57735,-0.57735;2.0944rad)
  Placement2 = pos=(-202,-2.018e-13,-2.018e-13) rot=(-0.57735,-0.57735,-0.57735;4.18879rad)
  Reference1 = -> Assembly [SH027.Edge26,SH027.Edge26]
  Reference2 = -> Assembly [sway_motor_mount_front_plate_shaft_support.Edge26,sway_motor_mount_front_plate_shaft_support.Edge26]
FEATURE [App::Link] sway_motor_mount_side
  LinkPlacement = pos=(334.4,135.565,9.95) rot=(0,0,-1;1.5708rad)
  LinkedObject = -> <external sway_motor_mount_side.FCStd>#Body
  Placement = pos=(334.4,135.565,9.95) rot=(0,0,-1;1.5708rad)
FEATURE [App::Link] sway_motor_mount_top
  LinkPlacement = pos=(434,135.5,10) rot=(0,0,1;1.5708rad)
  LinkedObject = -> <external sway_motor_mount_top.FCStd>#Body
  Placement = pos=(434,135.5,10) rot=(0,0,1;1.5708rad)
FEATURE [App::FeaturePython] Joint032  label="Fixed_sway_motor_mount_top"  # Assembly joint (typed FeaturePython)
  Activated = true
  AngleMax = 0
  AngleMin = 0
  Detach1 = false
  Detach2 = false
  Distance = 0
  Distance2 = 0
  EnableAngleMax = false
  EnableAngleMin = false
  EnableLengthMax = false
  EnableLengthMin = false
  JointType = 0 (Fixed)
  LengthMax = 0
  LengthMin = 0
  Offset1 = pos=(0,-0.4,0) rot=(0,0,1;0rad)
  Offset2 = pos=(0,0,0) rot=(0,0,1;1.5708rad)
  Placement1 = pos=(1.95e-14,40.4,-106.6) rot=(-0.707107,0,0.707107;3.14159rad)
  Placement2 = pos=(0,-15,60.4) rot=(0.57735,-0.57735,0.57735;4.18879rad)
  Reference1 = -> Assembly [_0ST_M02438.Part__Feature006.Edge472,_0ST_M02438.Part__Feature006.Edge472]
  Reference2 = -> Assembly [sway_motor_mount_top.Edge23,sway_motor_mount_top.Edge23]
FEATURE [App::Link] sway_motor_mount_bottom
  LinkPlacement = pos=(419,135.5,10) rot=(0,0,-1;1.5708rad)
  LinkedObject = -> <external sway_motor_mount_bottom.FCStd>#Body
  Placement = pos=(419,135.5,10) rot=(0,0,-1;1.5708rad)
FEATURE [App::FeaturePython] Joint033  label="Fixed_sway_motor_mount_bottom"  # Assembly joint (typed FeaturePython)
  Activated = true
  AngleMax = 0
  AngleMin = 0
  Detach1 = false
  Detach2 = false
  Distance = 0
  Distance2 = 0
  EnableAngleMax = false
  EnableAngleMin = false
  EnableLengthMax = false
  EnableLengthMin = false
  JointType = 0 (Fixed)
  LengthMax = 0
  LengthMin = 0
  Offset1 = pos=(0.4,-30,0) rot=(0,0,1;0rad)
  Offset2 = pos=(0,0,0) rot=(0,0,-1;1.5708rad)
  Placement1 = pos=(0,30,-20) rot=(0.707107,0,0.707107;3.14159rad)
  Placement2 = pos=(2.629e-13,-40,-106.6) rot=(0.57735,0.57735,0.57735;2.0944rad)
  Reference1 = -> Assembly [sway_motor_mount_bottom.Edge11,sway_motor_mount_bottom.Edge11]
  Reference2 = -> Assembly [_0ST_M02438.Part__Feature006.Edge167,_0ST_M02438.Part__Feature006.Edge167]
FEATURE [App::FeaturePython] Joint034  label="Fixed_sway_motor_mount_side"  # Assembly joint (typed FeaturePython)
  Activated = true
  AngleMax = 0
  AngleMin = 0
  Detach1 = false
  Detach2 = false
  Distance = 0
  Distance2 = 0
  EnableAngleMax = false
  EnableAngleMin = false
  EnableLengthMax = false
  EnableLengthMin = false
  JointType = 0 (Fixed)
  LengthMax = 0
  LengthMin = 0
  Placement1 = pos=(-31.75,0,51.75) rot=(1,0,0;1.5708rad)
  Placement2 = pos=(-31.815,31.7,8) rot=(0,0,1;0rad)
  Reference1 = -> Assembly [sway_motor_mount_side.Edge399,sway_motor_mount_side.Edge399]
  Reference2 = -> Assembly [_0ST_M02438.Part__Feature003.Edge20,_0ST_M02438.Part__Feature003.Edge20]
FEATURE [Assembly::JointGroup] Joints
  Group = -> [GroundedJoint,Joint,Joint003,Joint004,Joint007,Joint008,Joint011,Joint012,Joint013,Joint014,Joint015,Joint016,Joint017,Joint018,Joint019,Joint020,Joint022,Joint023,Joint024,Joint025,Joint026,Joint027,Joint028,Joint029,Joint030,Joint032,Joint033,Joint034]
FEATURE [Assembly::AssemblyObject] Assembly  label="sway_platform"
  Group = -> [Joints,SC25UU_to_SH25,SC25UU_to_SH026,GroundedJoint,Joint,SC25UU,SC25UU001,SC25UU002,SC25UU003,Joint003,Joint004,SH25,SH026,SH027,SH028,Joint007,Joint008,linear_shaft_25x428,linear_shaft_25x429,Joint011,Joint012,SH029,Joint013,DSG16H_to_SH25,Joint014,DSG16H,Joint015,SFU1605_ball_screw_nut,Joint016,_0ST_M02438,Joint017,coupler_10x19,Joint018,SFU1605_ball_screw_250mm,Joint019,BK12,Joint020,+20 more]
  Origin = -> Origin
  Type = Assembly
